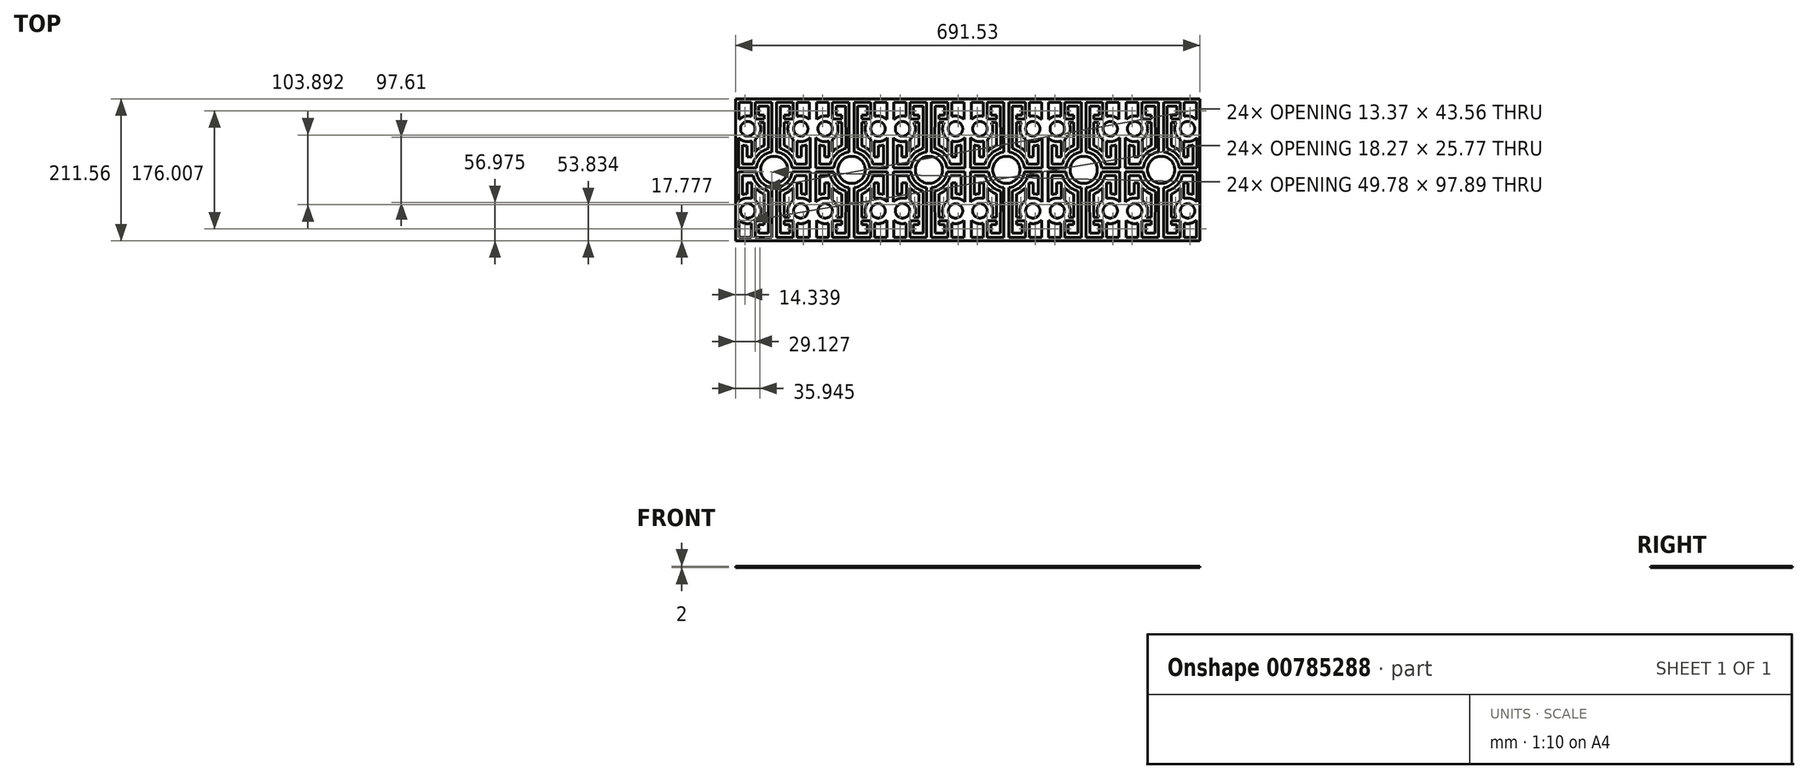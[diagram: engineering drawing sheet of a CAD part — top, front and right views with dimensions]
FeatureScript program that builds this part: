
annotation { "Feature Type Name" : "Feature", "Feature Type Description" : "" }
export const myFeature = defineFeature(function(context is Context, id is Id, definition is map)
    precondition{}
    {
        {
            var Q0;
            Q0=qCreatedBy(makeId("Top.planeOp"),FACE);
            var sketch = newSketch(context, id + "F0", { "sketchPlane" : qUnion([Q0])});
            skLineSegment(sketch, "E0.MirrorCS", {"start": v(61.19, -105.78) * mm, "end": v(-54.07, -105.78) * mm});
            skLineSegment(sketch, "E1.MirrorCS", {"start": v(-54.07, -105.78) * mm, "end": v(-54.07, 105.78) * mm});
            skLineSegment(sketch, "E2.MirrorCS", {"start": v(-54.07, 105.78) * mm, "end": v(-54.07, -105.78) * mm});
            skLineSegment(sketch, "E3.MirrorCS", {"start": v(61.19, 105.78) * mm, "end": v(-54.07, 105.78) * mm});
            skLineSegment(sketch, "E4.MirrorCS", {"start": v(-11.44, 75.88) * mm, "end": v(-11.44, 81.85) * mm});
            skLineSegment(sketch, "E5.MirrorCS", {"start": v(18.56, -75.88) * mm, "end": v(31.94, -75.88) * mm});
            skLineSegment(sketch, "E6.MirrorCS", {"start": v(-36.6, -19.6) * mm, "end": v(-30.12, -19.6) * mm});
            skArc(sketch, "E7.MirrorCS", {"start": v(43.73, 35.72) * mm, "mid": v(47.48, 36.1) * mm, "end": v(51.14, 37.04) * mm});
            skLineSegment(sketch, "E8.MirrorCS", {"start": v(43.73, 19.6) * mm, "end": v(37.24, 19.6) * mm});
            skLineSegment(sketch, "E9.MirrorCS", {"start": v(-19.53, 70.59) * mm, "end": v(-11.44, 70.59) * mm});
            skLineSegment(sketch, "E10.MirrorCS", {"start": v(-36.6, 19.6) * mm, "end": v(-30.12, 19.6) * mm});
            skArc(sketch, "E11.MirrorCS", {"start": v(43.73, -35.72) * mm, "mid": v(47.48, -36.1) * mm, "end": v(51.14, -37.04) * mm});
            skLineSegment(sketch, "E12.MirrorCS", {"start": v(-11.44, 75.88) * mm, "end": v(-24.82, 75.88) * mm});
            skArc(sketch, "E13.MirrorCS", {"start": v(-36.6, 35.72) * mm, "mid": v(-40.36, 36.1) * mm, "end": v(-44.02, 37.04) * mm});
            skLineSegment(sketch, "E14.MirrorCS", {"start": v(18.56, 75.88) * mm, "end": v(31.94, 75.88) * mm});
            skLineSegment(sketch, "E15.MirrorCS", {"start": v(31.94, -100.89) * mm, "end": v(31.94, -75.88) * mm});
            skLineSegment(sketch, "E16.MirrorCS", {"start": v(18.56, 75.88) * mm, "end": v(18.56, 81.85) * mm});
            skLineSegment(sketch, "E17.MirrorCS", {"start": v(-11.44, -75.88) * mm, "end": v(-11.44, -81.85) * mm});
            skLineSegment(sketch, "E18.MirrorCS", {"start": v(26.65, 70.59) * mm, "end": v(18.56, 70.59) * mm});
            skLineSegment(sketch, "E19.MirrorCS", {"start": v(26.67, 81.85) * mm, "end": v(18.56, 81.85) * mm});
            skLineSegment(sketch, "E20.MirrorCS", {"start": v(-19.55, -81.85) * mm, "end": v(-11.44, -81.85) * mm});
            skLineSegment(sketch, "E21.MirrorCS", {"start": v(18.56, -75.88) * mm, "end": v(18.56, -81.85) * mm});
            skLineSegment(sketch, "E22.MirrorCS", {"start": v(-19.53, -70.59) * mm, "end": v(-11.44, -70.59) * mm});
            skArc(sketch, "E23.MirrorCS", {"start": v(-36.6, -35.72) * mm, "mid": v(-40.36, -36.1) * mm, "end": v(-44.02, -37.04) * mm});
            skLineSegment(sketch, "E24.MirrorCS", {"start": v(-11.44, -75.88) * mm, "end": v(-24.82, -75.88) * mm});
            skLineSegment(sketch, "E25.MirrorCS", {"start": v(-19.55, -81.85) * mm, "end": v(-19.55, -94.64) * mm});
            skLineSegment(sketch, "E26.MirrorCS", {"start": v(-19.55, 94.64) * mm, "end": v(-5.34, 94.64) * mm});
            skLineSegment(sketch, "E27.MirrorCS", {"start": v(26.67, -81.85) * mm, "end": v(26.67, -94.64) * mm});
            skLineSegment(sketch, "E28.MirrorCS", {"start": v(-19.55, -94.64) * mm, "end": v(-5.34, -94.64) * mm});
            skLineSegment(sketch, "E29.MirrorCS", {"start": v(-19.55, 81.85) * mm, "end": v(-11.44, 81.85) * mm});
            skLineSegment(sketch, "E30.MirrorCS", {"start": v(26.67, 81.85) * mm, "end": v(26.67, 94.64) * mm});
            skLineSegment(sketch, "E31.MirrorCS", {"start": v(-19.55, 81.85) * mm, "end": v(-19.55, 94.64) * mm});
            skLineSegment(sketch, "E32.MirrorCS", {"start": v(43.73, -19.6) * mm, "end": v(37.24, -19.6) * mm});
            skLineSegment(sketch, "E33.MirrorCS", {"start": v(31.94, 100.89) * mm, "end": v(31.94, 75.88) * mm});
            skLineSegment(sketch, "E34.MirrorCS", {"start": v(26.65, -70.59) * mm, "end": v(18.56, -70.59) * mm});
            skLineSegment(sketch, "E35.MirrorCS", {"start": v(26.67, -81.85) * mm, "end": v(18.56, -81.85) * mm});
            skLineSegment(sketch, "E36.MirrorCS", {"start": v(-48.87, 100.89) * mm, "end": v(-30.6, 100.89) * mm});
            skArc(sketch, "E37.MirrorCS", {"start": v(-30.6, 79.48) * mm, "mid": v(-40.3, 79.71) * mm, "end": v(-48.87, 75.12) * mm});
            skLineSegment(sketch, "E38.MirrorCS", {"start": v(-30.6, 79.48) * mm, "end": v(-30.6, 100.89) * mm});
            skLineSegment(sketch, "E39.MirrorCS", {"start": v(-24.82, 100.89) * mm, "end": v(-24.82, 75.88) * mm});
            skLineSegment(sketch, "E40.MirrorCS", {"start": v(31.94, 100.89) * mm, "end": v(7.17, 100.89) * mm});
            skLineSegment(sketch, "E41.MirrorCS", {"start": v(-24.82, -100.89) * mm, "end": v(-24.82, -75.88) * mm});
            skLineSegment(sketch, "E42.MirrorCS", {"start": v(37.24, 42.87) * mm, "end": v(37.24, 19.6) * mm});
            skArc(sketch, "E43.MirrorCS", {"start": v(18.56, -36.2) * mm, "mid": v(25.73, -32.32) * mm, "end": v(31.93, -27.02) * mm});
            skLineSegment(sketch, "E44.MirrorCS", {"start": v(56.95, -47.98) * mm, "end": v(56.95, -3) * mm});
            skCircle(sketch, "E45.MirrorC", {"center": v(-35.89, 61.2) * mm, "radius": 10.77 * mm});
            skLineSegment(sketch, "E46.MirrorCS", {"start": v(-30.6, -79.48) * mm, "end": v(-30.6, -100.89) * mm});
            skLineSegment(sketch, "E47.MirrorCS", {"start": v(-30.12, 42.87) * mm, "end": v(-30.12, 19.6) * mm});
            skArc(sketch, "E48.MirrorCS", {"start": v(35.31, 8.78) * mm, "mid": v(26.82, 23.35) * mm, "end": v(12.23, 31.82) * mm});
            skLineSegment(sketch, "E49.MirrorCS", {"start": v(-0.05, -26.62) * mm, "end": v(-0.05, -100.89) * mm});
            skArc(sketch, "E50.MirrorCS", {"start": v(7.17, -26.62) * mm, "mid": v(22.75, -18.77) * mm, "end": v(30.21, -3) * mm});
            skLineSegment(sketch, "E51.MirrorCS", {"start": v(26.67, 94.64) * mm, "end": v(12.46, 94.64) * mm});
            skLineSegment(sketch, "E52.MirrorCS", {"start": v(-28.2, 8.78) * mm, "end": v(-44.02, 8.78) * mm});
            skLineSegment(sketch, "E53.MirrorCS", {"start": v(55.99, 100.89) * mm, "end": v(37.72, 100.89) * mm});
            skLineSegment(sketch, "E54.MirrorCS", {"start": v(43.73, 19.6) * mm, "end": v(43.73, 35.72) * mm});
            skLineSegment(sketch, "E55.MirrorCS", {"start": v(30.21, -3) * mm, "end": v(56.95, -3) * mm});
            skArc(sketch, "E56.MirrorCS", {"start": v(37.72, 79.48) * mm, "mid": v(47.43, 79.71) * mm, "end": v(55.99, 75.12) * mm});
            skLineSegment(sketch, "E57.MirrorCS", {"start": v(-24.82, -100.89) * mm, "end": v(-0.05, -100.89) * mm});
            skLineSegment(sketch, "E58.MirrorCS", {"start": v(-11.44, 70.59) * mm, "end": v(-11.44, 36.2) * mm});
            skLineSegment(sketch, "E59.MirrorCS", {"start": v(12.46, 94.64) * mm, "end": v(12.23, 31.81) * mm});
            skArc(sketch, "E60.MirrorCS", {"start": v(-24.81, 45.33) * mm, "mid": v(-17.03, 56.84) * mm, "end": v(-18.96, 70.59) * mm});
            skLineSegment(sketch, "E61.MirrorCS", {"start": v(-5.34, 94.64) * mm, "end": v(-5.1, 31.81) * mm});
            skLineSegment(sketch, "E62.MirrorCS", {"start": v(35.31, -8.78) * mm, "end": v(51.14, -8.78) * mm});
            skArc(sketch, "E63.MirrorCS", {"start": v(-28.2, 8.78) * mm, "mid": v(-19.7, 23.35) * mm, "end": v(-5.1, 31.82) * mm});
            skLineSegment(sketch, "E64.MirrorCS", {"start": v(37.72, -79.48) * mm, "end": v(37.72, -100.89) * mm});
            skLineSegment(sketch, "E65.MirrorCS", {"start": v(-24.81, -27.02) * mm, "end": v(-24.81, -45.33) * mm});
            skCircle(sketch, "E66.MirrorC", {"center": v(43, -61.2) * mm, "radius": 10.77 * mm});
            skLineSegment(sketch, "E67.MirrorCS", {"start": v(31.94, -100.89) * mm, "end": v(7.17, -100.89) * mm});
            skLineSegment(sketch, "E68.MirrorCS", {"start": v(-48.87, -100.89) * mm, "end": v(-30.6, -100.89) * mm});
            skLineSegment(sketch, "E69.MirrorCS", {"start": v(-30.12, -42.87) * mm, "end": v(-30.12, -19.6) * mm});
            skLineSegment(sketch, "E70.MirrorCS", {"start": v(51.14, -37.04) * mm, "end": v(51.14, -8.78) * mm});
            skLineSegment(sketch, "E71.MirrorCS", {"start": v(51.14, 37.04) * mm, "end": v(51.14, 8.78) * mm});
            skLineSegment(sketch, "E72.MirrorCS", {"start": v(7.17, 26.62) * mm, "end": v(7.17, 100.89) * mm});
            skLineSegment(sketch, "E73.MirrorCS", {"start": v(-24.81, 27.02) * mm, "end": v(-24.81, 45.33) * mm});
            skLineSegment(sketch, "E74.MirrorCS", {"start": v(-36.6, 19.6) * mm, "end": v(-36.6, 35.72) * mm});
            skLineSegment(sketch, "E75.MirrorCS", {"start": v(56.95, 47.98) * mm, "end": v(56.95, 3) * mm});
            skLineSegment(sketch, "E76.MirrorCS", {"start": v(55.99, -75.12) * mm, "end": v(55.99, -100.89) * mm});
            skArc(sketch, "E77.MirrorCS", {"start": v(-11.44, 36.2) * mm, "mid": v(-18.6, 32.32) * mm, "end": v(-24.81, 27.02) * mm});
            skArc(sketch, "E78.MirrorCS", {"start": v(-0.05, 26.62) * mm, "mid": v(-15.63, 18.77) * mm, "end": v(-23.1, 3) * mm});
            skLineSegment(sketch, "E79.MirrorCS", {"start": v(55.99, 75.12) * mm, "end": v(55.99, 100.89) * mm});
            skArc(sketch, "E80.MirrorCS", {"start": v(31.93, 45.33) * mm, "mid": v(24.15, 56.84) * mm, "end": v(26.08, 70.59) * mm});
            skLineSegment(sketch, "E81.MirrorCS", {"start": v(-24.82, 100.89) * mm, "end": v(-0.05, 100.89) * mm});
            skLineSegment(sketch, "E82.MirrorCS", {"start": v(-5.34, -94.64) * mm, "end": v(-5.1, -31.81) * mm});
            skLineSegment(sketch, "E83.MirrorCS", {"start": v(31.93, 27.02) * mm, "end": v(31.93, 45.33) * mm});
            skArc(sketch, "E84.MirrorCS", {"start": v(35.31, -8.78) * mm, "mid": v(26.82, -23.35) * mm, "end": v(12.23, -31.82) * mm});
            skArc(sketch, "E85.MirrorCS", {"start": v(7.17, 26.62) * mm, "mid": v(22.75, 18.77) * mm, "end": v(30.21, 3) * mm});
            skArc(sketch, "E86.MirrorCS", {"start": v(-24.81, -45.33) * mm, "mid": v(-17.03, -56.84) * mm, "end": v(-18.96, -70.59) * mm});
            skCircle(sketch, "E87.MirrorC", {"center": v(-35.89, -61.2) * mm, "radius": 10.77 * mm});
            skArc(sketch, "E88.MirrorCS", {"start": v(56.95, 47.98) * mm, "mid": v(47.83, 42.6) * mm, "end": v(37.24, 42.87) * mm});
            skLineSegment(sketch, "E89.MirrorCS", {"start": v(37.24, -42.87) * mm, "end": v(37.24, -19.6) * mm});
            skLineSegment(sketch, "E90.MirrorCS", {"start": v(-23.1, 3) * mm, "end": v(-49.83, 3) * mm});
            skLineSegment(sketch, "E91.MirrorCS", {"start": v(55.99, -100.89) * mm, "end": v(37.72, -100.89) * mm});
            skLineSegment(sketch, "E92.MirrorCS", {"start": v(-48.87, 75.12) * mm, "end": v(-48.87, 100.89) * mm});
            skLineSegment(sketch, "E93.MirrorCS", {"start": v(37.72, 79.48) * mm, "end": v(37.72, 100.89) * mm});
            skLineSegment(sketch, "E94.MirrorCS", {"start": v(-23.1, -3) * mm, "end": v(-49.83, -3) * mm});
            skArc(sketch, "E95.MirrorCS", {"start": v(37.72, -79.48) * mm, "mid": v(47.43, -79.71) * mm, "end": v(55.99, -75.12) * mm});
            skLineSegment(sketch, "E96.MirrorCS", {"start": v(43.73, -19.6) * mm, "end": v(43.73, -35.72) * mm});
            skLineSegment(sketch, "E97.MirrorCS", {"start": v(-49.83, 47.98) * mm, "end": v(-49.83, 3) * mm});
            skArc(sketch, "E98.MirrorCS", {"start": v(56.95, -47.98) * mm, "mid": v(47.83, -42.6) * mm, "end": v(37.24, -42.87) * mm});
            skLineSegment(sketch, "E99.MirrorCS", {"start": v(7.17, -26.62) * mm, "end": v(7.17, -100.89) * mm});
            skLineSegment(sketch, "E100.MirrorCS", {"start": v(12.46, -94.64) * mm, "end": v(12.23, -31.81) * mm});
            skLineSegment(sketch, "E101.MirrorCS", {"start": v(-44.02, -37.04) * mm, "end": v(-44.02, -8.78) * mm});
            skArc(sketch, "E102.MirrorCS", {"start": v(18.56, 36.2) * mm, "mid": v(25.73, 32.32) * mm, "end": v(31.93, 27.02) * mm});
            skLineSegment(sketch, "E103.MirrorCS", {"start": v(35.31, 8.78) * mm, "end": v(51.14, 8.78) * mm});
            skLineSegment(sketch, "E104.MirrorCS", {"start": v(-36.6, -19.6) * mm, "end": v(-36.6, -35.72) * mm});
            skArc(sketch, "E105.MirrorCS", {"start": v(-11.44, -36.2) * mm, "mid": v(-18.6, -32.32) * mm, "end": v(-24.81, -27.02) * mm});
            skLineSegment(sketch, "E106.MirrorCS", {"start": v(-28.2, -8.78) * mm, "end": v(-44.02, -8.78) * mm});
            skLineSegment(sketch, "E107.MirrorCS", {"start": v(-11.44, -70.59) * mm, "end": v(-11.44, -36.2) * mm});
            skLineSegment(sketch, "E108.MirrorCS", {"start": v(-49.83, -47.98) * mm, "end": v(-49.83, -3) * mm});
            skCircle(sketch, "E109.MirrorC", {"center": v(43, 61.2) * mm, "radius": 10.77 * mm});
            skLineSegment(sketch, "E110.MirrorCS", {"start": v(26.67, -94.64) * mm, "end": v(12.46, -94.64) * mm});
            skLineSegment(sketch, "E111.MirrorCS", {"start": v(-44.02, 37.04) * mm, "end": v(-44.02, 8.78) * mm});
            skArc(sketch, "E112.MirrorCS", {"start": v(31.93, -45.33) * mm, "mid": v(24.15, -56.84) * mm, "end": v(26.08, -70.59) * mm});
            skArc(sketch, "E113.MirrorCS", {"start": v(-49.83, -47.98) * mm, "mid": v(-40.7, -42.6) * mm, "end": v(-30.12, -42.87) * mm});
            skLineSegment(sketch, "E114.MirrorCS", {"start": v(-48.87, -75.12) * mm, "end": v(-48.87, -100.89) * mm});
            skArc(sketch, "E115.MirrorCS", {"start": v(-0.05, -26.62) * mm, "mid": v(-15.63, -18.77) * mm, "end": v(-23.1, -3) * mm});
            skLineSegment(sketch, "E116.MirrorCS", {"start": v(18.56, 70.59) * mm, "end": v(18.56, 36.2) * mm});
            skArc(sketch, "E117.MirrorCS", {"start": v(-30.6, -79.48) * mm, "mid": v(-40.3, -79.71) * mm, "end": v(-48.87, -75.12) * mm});
            skLineSegment(sketch, "E118.MirrorCS", {"start": v(30.21, 3) * mm, "end": v(56.95, 3) * mm});
            skLineSegment(sketch, "E119.MirrorCS", {"start": v(18.56, -70.59) * mm, "end": v(18.56, -36.2) * mm});
            skLineSegment(sketch, "E120.MirrorCS", {"start": v(31.93, -27.02) * mm, "end": v(31.93, -45.33) * mm});
            skArc(sketch, "E121.MirrorCS", {"start": v(-49.83, 47.98) * mm, "mid": v(-40.7, 42.6) * mm, "end": v(-30.12, 42.87) * mm});
            skArc(sketch, "E122.MirrorCS", {"start": v(-28.2, -8.78) * mm, "mid": v(-19.7, -23.35) * mm, "end": v(-5.1, -31.82) * mm});
            skLineSegment(sketch, "E123.MirrorCS", {"start": v(-0.05, 26.62) * mm, "end": v(-0.05, 100.89) * mm});
            skCircle(sketch, "E124.MirrorC", {"center": v(3.56, 0) * mm, "radius": 20.2 * mm});
            skLineSegment(sketch, "E125.MirrorCS", {"start": v(-284.58, 105.78) * mm, "end": v(-284.58, -105.78) * mm});
            skLineSegment(sketch, "E126.MirrorCS", {"start": v(-284.58, -105.78) * mm, "end": v(-284.58, 105.78) * mm});
            skLineSegment(sketch, "E127.MirrorCS", {"start": v(-241.95, 75.88) * mm, "end": v(-241.95, 81.85) * mm});
            skLineSegment(sketch, "E128.MirrorCS", {"start": v(-211.95, 75.88) * mm, "end": v(-211.95, 81.85) * mm});
            skLineSegment(sketch, "E129.MirrorCS", {"start": v(-126.7, 75.88) * mm, "end": v(-126.7, 81.85) * mm});
            skLineSegment(sketch, "E130.MirrorCS", {"start": v(-241.95, -75.88) * mm, "end": v(-241.95, -81.85) * mm});
            skLineSegment(sketch, "E131.MirrorCS", {"start": v(-71.53, -19.6) * mm, "end": v(-78.02, -19.6) * mm});
            skLineSegment(sketch, "E132.MirrorCS", {"start": v(-255.33, -100.89) * mm, "end": v(-255.33, -75.88) * mm});
            skArc(sketch, "E133.MirrorCS", {"start": v(-71.53, 35.72) * mm, "mid": v(-67.77, 36.1) * mm, "end": v(-64.11, 37.04) * mm});
            skLineSegment(sketch, "E134.MirrorCS", {"start": v(-134.8, 81.85) * mm, "end": v(-126.7, 81.85) * mm});
            skArc(sketch, "E135.MirrorCS", {"start": v(-151.86, 35.72) * mm, "mid": v(-155.62, 36.1) * mm, "end": v(-159.28, 37.04) * mm});
            skLineSegment(sketch, "E136.MirrorCS", {"start": v(-250.06, -81.85) * mm, "end": v(-250.06, -94.64) * mm});
            skLineSegment(sketch, "E137.MirrorCS", {"start": v(-71.53, 19.6) * mm, "end": v(-78.02, 19.6) * mm});
            skLineSegment(sketch, "E138.MirrorCS", {"start": v(-88.6, 70.59) * mm, "end": v(-96.7, 70.59) * mm});
            skArc(sketch, "E139.MirrorCS", {"start": v(-71.53, -35.72) * mm, "mid": v(-67.77, -36.1) * mm, "end": v(-64.11, -37.04) * mm});
            skArc(sketch, "E140.MirrorCS", {"start": v(-151.86, -35.72) * mm, "mid": v(-155.62, -36.1) * mm, "end": v(-159.28, -37.04) * mm});
            skLineSegment(sketch, "E141.MirrorCS", {"start": v(-134.8, -81.85) * mm, "end": v(-126.7, -81.85) * mm});
            skLineSegment(sketch, "E142.MirrorCS", {"start": v(-126.7, -75.88) * mm, "end": v(-126.7, -81.85) * mm});
            skLineSegment(sketch, "E143.MirrorCS", {"start": v(-186.78, 19.6) * mm, "end": v(-193.27, 19.6) * mm});
            skLineSegment(sketch, "E144.MirrorCS", {"start": v(-203.84, -81.85) * mm, "end": v(-203.84, -94.64) * mm});
            skArc(sketch, "E145.MirrorCS", {"start": v(-267.12, 35.72) * mm, "mid": v(-270.87, 36.1) * mm, "end": v(-274.53, 37.04) * mm});
            skLineSegment(sketch, "E146.MirrorCS", {"start": v(-211.95, -75.88) * mm, "end": v(-211.95, -81.85) * mm});
            skArc(sketch, "E147.MirrorCS", {"start": v(-267.12, -35.72) * mm, "mid": v(-270.87, -36.1) * mm, "end": v(-274.53, -37.04) * mm});
            skLineSegment(sketch, "E148.MirrorCS", {"start": v(-134.79, 70.59) * mm, "end": v(-126.7, 70.59) * mm});
            skLineSegment(sketch, "E149.MirrorCS", {"start": v(-96.7, -75.88) * mm, "end": v(-83.31, -75.88) * mm});
            skLineSegment(sketch, "E150.MirrorCS", {"start": v(-88.6, -70.59) * mm, "end": v(-96.7, -70.59) * mm});
            skLineSegment(sketch, "E151.MirrorCS", {"start": v(-96.7, -75.88) * mm, "end": v(-96.7, -81.85) * mm});
            skLineSegment(sketch, "E152.MirrorCS", {"start": v(-134.8, -81.85) * mm, "end": v(-134.8, -94.64) * mm});
            skLineSegment(sketch, "E153.MirrorCS", {"start": v(-88.58, -81.85) * mm, "end": v(-88.58, -94.64) * mm});
            skLineSegment(sketch, "E154.MirrorCS", {"start": v(-151.86, -19.6) * mm, "end": v(-145.37, -19.6) * mm});
            skLineSegment(sketch, "E155.MirrorCS", {"start": v(-126.7, -75.88) * mm, "end": v(-140.08, -75.88) * mm});
            skLineSegment(sketch, "E156.MirrorCS", {"start": v(-96.7, 75.88) * mm, "end": v(-96.7, 81.85) * mm});
            skArc(sketch, "E157.MirrorCS", {"start": v(-186.78, -35.72) * mm, "mid": v(-183.03, -36.1) * mm, "end": v(-179.37, -37.04) * mm});
            skLineSegment(sketch, "E158.MirrorCS", {"start": v(-88.58, -81.85) * mm, "end": v(-96.7, -81.85) * mm});
            skLineSegment(sketch, "E159.MirrorCS", {"start": v(-134.79, -70.59) * mm, "end": v(-126.7, -70.59) * mm});
            skLineSegment(sketch, "E160.MirrorCS", {"start": v(-250.06, -81.85) * mm, "end": v(-241.95, -81.85) * mm});
            skArc(sketch, "E161.MirrorCS", {"start": v(-186.78, 35.72) * mm, "mid": v(-183.03, 36.1) * mm, "end": v(-179.37, 37.04) * mm});
            skLineSegment(sketch, "E162.MirrorCS", {"start": v(-186.78, -19.6) * mm, "end": v(-193.27, -19.6) * mm});
            skLineSegment(sketch, "E163.MirrorCS", {"start": v(-96.7, 75.88) * mm, "end": v(-83.31, 75.88) * mm});
            skLineSegment(sketch, "E164.MirrorCS", {"start": v(-198.57, -100.89) * mm, "end": v(-198.57, -75.88) * mm});
            skLineSegment(sketch, "E165.MirrorCS", {"start": v(-126.7, 75.88) * mm, "end": v(-140.08, 75.88) * mm});
            skLineSegment(sketch, "E166.MirrorCS", {"start": v(-88.58, 81.85) * mm, "end": v(-96.7, 81.85) * mm});
            skLineSegment(sketch, "E167.MirrorCS", {"start": v(-151.86, 19.6) * mm, "end": v(-145.37, 19.6) * mm});
            skLineSegment(sketch, "E168.MirrorCS", {"start": v(-203.84, -81.85) * mm, "end": v(-211.95, -81.85) * mm});
            skLineSegment(sketch, "E169.MirrorCS", {"start": v(-267.12, 19.6) * mm, "end": v(-260.63, 19.6) * mm});
            skLineSegment(sketch, "E170.MirrorCS", {"start": v(-267.12, -19.6) * mm, "end": v(-260.63, -19.6) * mm});
            skLineSegment(sketch, "E171.MirrorCS", {"start": v(-250.06, 81.85) * mm, "end": v(-241.95, 81.85) * mm});
            skLineSegment(sketch, "E172.MirrorCS", {"start": v(-203.84, 81.85) * mm, "end": v(-211.95, 81.85) * mm});
            skLineSegment(sketch, "E173.MirrorCS", {"start": v(-211.95, 75.88) * mm, "end": v(-198.57, 75.88) * mm});
            skLineSegment(sketch, "E174.MirrorCS", {"start": v(-211.95, -75.88) * mm, "end": v(-198.57, -75.88) * mm});
            skLineSegment(sketch, "E175.MirrorCS", {"start": v(-203.86, 70.59) * mm, "end": v(-211.95, 70.59) * mm});
            skLineSegment(sketch, "E176.MirrorCS", {"start": v(-203.86, -70.59) * mm, "end": v(-211.95, -70.59) * mm});
            skLineSegment(sketch, "E177.MirrorCS", {"start": v(-250.04, -70.59) * mm, "end": v(-241.95, -70.59) * mm});
            skLineSegment(sketch, "E178.MirrorCS", {"start": v(-241.95, -75.88) * mm, "end": v(-255.33, -75.88) * mm});
            skLineSegment(sketch, "E179.MirrorCS", {"start": v(-241.95, 75.88) * mm, "end": v(-255.33, 75.88) * mm});
            skLineSegment(sketch, "E180.MirrorCS", {"start": v(-250.04, 70.59) * mm, "end": v(-241.95, 70.59) * mm});
            skArc(sketch, "E181.MirrorCS", {"start": v(-108.08, -26.62) * mm, "mid": v(-92.5, -18.77) * mm, "end": v(-85.04, -3) * mm});
            skLineSegment(sketch, "E182.MirrorCS", {"start": v(-143.44, 8.78) * mm, "end": v(-159.28, 8.78) * mm});
            skLineSegment(sketch, "E183.MirrorCS", {"start": v(-102.8, -94.64) * mm, "end": v(-103.03, -31.81) * mm});
            skLineSegment(sketch, "E184.MirrorCS", {"start": v(-88.58, 94.64) * mm, "end": v(-102.8, 94.64) * mm});
            skLineSegment(sketch, "E185.MirrorCS", {"start": v(-159.28, 37.04) * mm, "end": v(-159.28, 8.78) * mm});
            skArc(sketch, "E186.MirrorCS", {"start": v(-192.8, 79.48) * mm, "mid": v(-183.08, 79.71) * mm, "end": v(-174.52, 75.12) * mm});
            skLineSegment(sketch, "E187.MirrorCS", {"start": v(-174.52, 100.89) * mm, "end": v(-192.8, 100.89) * mm});
            skLineSegment(sketch, "E188.MirrorCS", {"start": v(-85.04, 3) * mm, "end": v(-58.3, 3) * mm});
            skLineSegment(sketch, "E189.MirrorCS", {"start": v(-218.05, 94.64) * mm, "end": v(-218.28, 31.81) * mm});
            skLineSegment(sketch, "E190.MirrorCS", {"start": v(-241.95, -70.59) * mm, "end": v(-241.95, -36.2) * mm});
            skLineSegment(sketch, "E191.MirrorCS", {"start": v(-134.8, 81.85) * mm, "end": v(-134.8, 94.64) * mm});
            skLineSegment(sketch, "E192.MirrorCS", {"start": v(-140.08, 100.89) * mm, "end": v(-115.3, 100.89) * mm});
            skArc(sketch, "E193.MirrorCS", {"start": v(-241.95, -36.2) * mm, "mid": v(-249.12, -32.32) * mm, "end": v(-255.32, -27.02) * mm});
            skLineSegment(sketch, "E194.MirrorCS", {"start": v(-260.63, -42.87) * mm, "end": v(-260.63, -19.6) * mm});
            skLineSegment(sketch, "E195.MirrorCS", {"start": v(-211.95, 70.59) * mm, "end": v(-211.95, 36.2) * mm});
            skLineSegment(sketch, "E196.MirrorCS", {"start": v(-235.85, -94.64) * mm, "end": v(-235.62, -31.81) * mm});
            skLineSegment(sketch, "E197.MirrorCS", {"start": v(-230.56, -26.62) * mm, "end": v(-230.56, -100.89) * mm});
            skCircle(sketch, "E198.MirrorC", {"center": v(-187.5, 61.2) * mm, "radius": 10.77 * mm});
            skArc(sketch, "E199.MirrorCS", {"start": v(-77.54, 79.48) * mm, "mid": v(-67.83, 79.71) * mm, "end": v(-59.27, 75.12) * mm});
            skLineSegment(sketch, "E200.MirrorCS", {"start": v(-88.58, 81.85) * mm, "end": v(-88.58, 94.64) * mm});
            skCircle(sketch, "E201.MirrorC", {"center": v(-266.4, -61.2) * mm, "radius": 10.77 * mm});
            skLineSegment(sketch, "E202.MirrorCS", {"start": v(-258.7, 8.78) * mm, "end": v(-274.53, 8.78) * mm});
            skLineSegment(sketch, "E203.MirrorCS", {"start": v(-140.08, -100.89) * mm, "end": v(-140.08, -75.88) * mm});
            skArc(sketch, "E204.MirrorCS", {"start": v(-255.32, 45.33) * mm, "mid": v(-247.54, 56.84) * mm, "end": v(-249.47, 70.59) * mm});
            skArc(sketch, "E205.MirrorCS", {"start": v(-173.55, 47.98) * mm, "mid": v(-182.68, 42.6) * mm, "end": v(-193.27, 42.87) * mm});
            skArc(sketch, "E206.MirrorCS", {"start": v(-258.7, -8.78) * mm, "mid": v(-250.2, -23.35) * mm, "end": v(-235.62, -31.82) * mm});
            skLineSegment(sketch, "E207.MirrorCS", {"start": v(-145.85, 79.48) * mm, "end": v(-145.85, 100.89) * mm});
            skArc(sketch, "E208.MirrorCS", {"start": v(-96.7, 36.2) * mm, "mid": v(-89.53, 32.32) * mm, "end": v(-83.32, 27.02) * mm});
            skLineSegment(sketch, "E209.MirrorCS", {"start": v(-102.8, 94.64) * mm, "end": v(-103.03, 31.81) * mm});
            skCircle(sketch, "E210.MirrorC", {"center": v(-72.25, 61.2) * mm, "radius": 10.77 * mm});
            skLineSegment(sketch, "E211.MirrorCS", {"start": v(-115.3, -26.62) * mm, "end": v(-115.3, -100.89) * mm});
            skLineSegment(sketch, "E212.MirrorCS", {"start": v(-186.78, -19.6) * mm, "end": v(-186.78, -35.72) * mm});
            skLineSegment(sketch, "E213.MirrorCS", {"start": v(-250.06, 94.64) * mm, "end": v(-235.85, 94.64) * mm});
            skArc(sketch, "E214.MirrorCS", {"start": v(-145.85, -79.48) * mm, "mid": v(-155.56, -79.71) * mm, "end": v(-164.12, -75.12) * mm});
            skLineSegment(sketch, "E215.MirrorCS", {"start": v(-164.12, -100.89) * mm, "end": v(-145.85, -100.89) * mm});
            skLineSegment(sketch, "E216.MirrorCS", {"start": v(-140.08, -100.89) * mm, "end": v(-115.3, -100.89) * mm});
            skLineSegment(sketch, "E217.MirrorCS", {"start": v(-59.27, -100.89) * mm, "end": v(-77.54, -100.89) * mm});
            skLineSegment(sketch, "E218.MirrorCS", {"start": v(-267.12, -19.6) * mm, "end": v(-267.12, -35.72) * mm});
            skLineSegment(sketch, "E219.MirrorCS", {"start": v(-198.57, 100.89) * mm, "end": v(-223.34, 100.89) * mm});
            skLineSegment(sketch, "E220.MirrorCS", {"start": v(-174.52, 75.12) * mm, "end": v(-174.52, 100.89) * mm});
            skLineSegment(sketch, "E221.MirrorCS", {"start": v(-138.35, 3) * mm, "end": v(-165.09, 3) * mm});
            skCircle(sketch, "E222.MirrorC", {"center": v(-72.25, -61.2) * mm, "radius": 10.77 * mm});
            skLineSegment(sketch, "E223.MirrorCS", {"start": v(-164.12, -75.12) * mm, "end": v(-164.12, -100.89) * mm});
            skLineSegment(sketch, "E224.MirrorCS", {"start": v(-140.07, -27.02) * mm, "end": v(-140.07, -45.33) * mm});
            skLineSegment(sketch, "E225.MirrorCS", {"start": v(-145.37, -42.87) * mm, "end": v(-145.37, -19.6) * mm});
            skLineSegment(sketch, "E226.MirrorCS", {"start": v(-280.34, -47.98) * mm, "end": v(-280.34, -3) * mm});
            skLineSegment(sketch, "E227.MirrorCS", {"start": v(-164.12, 75.12) * mm, "end": v(-164.12, 100.89) * mm});
            skArc(sketch, "E228.MirrorCS", {"start": v(-211.95, 36.2) * mm, "mid": v(-204.78, 32.32) * mm, "end": v(-198.58, 27.02) * mm});
            skArc(sketch, "E229.MirrorCS", {"start": v(-79.94, 8.78) * mm, "mid": v(-88.44, 23.35) * mm, "end": v(-103.03, 31.82) * mm});
            skLineSegment(sketch, "E230.MirrorCS", {"start": v(-78.02, 42.87) * mm, "end": v(-78.02, 19.6) * mm});
            skLineSegment(sketch, "E231.MirrorCS", {"start": v(-218.05, -94.64) * mm, "end": v(-218.28, -31.81) * mm});
            skLineSegment(sketch, "E232.MirrorCS", {"start": v(-151.86, 19.6) * mm, "end": v(-151.86, 35.72) * mm});
            skArc(sketch, "E233.MirrorCS", {"start": v(-145.85, 79.48) * mm, "mid": v(-155.56, 79.71) * mm, "end": v(-164.12, 75.12) * mm});
            skLineSegment(sketch, "E234.MirrorCS", {"start": v(-96.7, -70.59) * mm, "end": v(-96.7, -36.2) * mm});
            skLineSegment(sketch, "E235.MirrorCS", {"start": v(-64.11, 37.04) * mm, "end": v(-64.11, 8.78) * mm});
            skLineSegment(sketch, "E236.MirrorCS", {"start": v(-138.35, -3) * mm, "end": v(-165.09, -3) * mm});
            skLineSegment(sketch, "E237.MirrorCS", {"start": v(-165.09, 47.98) * mm, "end": v(-165.09, 3) * mm});
            skLineSegment(sketch, "E238.MirrorCS", {"start": v(-200.3, -3) * mm, "end": v(-173.55, -3) * mm});
            skArc(sketch, "E239.MirrorCS", {"start": v(-241.95, 36.2) * mm, "mid": v(-249.12, 32.32) * mm, "end": v(-255.32, 27.02) * mm});
            skLineSegment(sketch, "E240.MirrorCS", {"start": v(-83.32, 27.02) * mm, "end": v(-83.32, 45.33) * mm});
            skLineSegment(sketch, "E241.MirrorCS", {"start": v(-261.1, 79.48) * mm, "end": v(-261.1, 100.89) * mm});
            skArc(sketch, "E242.MirrorCS", {"start": v(-173.55, -47.98) * mm, "mid": v(-182.68, -42.6) * mm, "end": v(-193.27, -42.87) * mm});
            skLineSegment(sketch, "E243.MirrorCS", {"start": v(-255.33, 100.89) * mm, "end": v(-230.56, 100.89) * mm});
            skLineSegment(sketch, "E244.MirrorCS", {"start": v(-250.06, -94.64) * mm, "end": v(-235.85, -94.64) * mm});
            skArc(sketch, "E245.MirrorCS", {"start": v(-192.8, -79.48) * mm, "mid": v(-183.08, -79.71) * mm, "end": v(-174.52, -75.12) * mm});
            skLineSegment(sketch, "E246.MirrorCS", {"start": v(-203.84, -94.64) * mm, "end": v(-218.05, -94.64) * mm});
            skLineSegment(sketch, "E247.MirrorCS", {"start": v(-230.56, 26.62) * mm, "end": v(-230.56, 100.89) * mm});
            skArc(sketch, "E248.MirrorCS", {"start": v(-115.3, 26.62) * mm, "mid": v(-130.89, 18.77) * mm, "end": v(-138.35, 3) * mm});
            skLineSegment(sketch, "E249.MirrorCS", {"start": v(-59.27, 75.12) * mm, "end": v(-59.27, 100.89) * mm});
            skLineSegment(sketch, "E250.MirrorCS", {"start": v(-134.8, 94.64) * mm, "end": v(-120.6, 94.64) * mm});
            skLineSegment(sketch, "E251.MirrorCS", {"start": v(-140.07, 27.02) * mm, "end": v(-140.07, 45.33) * mm});
            skArc(sketch, "E252.MirrorCS", {"start": v(-195.2, 8.78) * mm, "mid": v(-203.69, 23.35) * mm, "end": v(-218.28, 31.82) * mm});
            skCircle(sketch, "E253.MirrorC", {"center": v(-187.5, -61.2) * mm, "radius": 10.77 * mm});
            skArc(sketch, "E254.MirrorCS", {"start": v(-230.56, -26.62) * mm, "mid": v(-246.14, -18.77) * mm, "end": v(-253.6, -3) * mm});
            skArc(sketch, "E255.MirrorCS", {"start": v(-280.34, -47.98) * mm, "mid": v(-271.22, -42.6) * mm, "end": v(-260.63, -42.87) * mm});
            skLineSegment(sketch, "E256.MirrorCS", {"start": v(-280.34, 47.98) * mm, "end": v(-280.34, 3) * mm});
            skLineSegment(sketch, "E257.MirrorCS", {"start": v(-179.37, -37.04) * mm, "end": v(-179.37, -8.78) * mm});
            skArc(sketch, "E258.MirrorCS", {"start": v(-280.34, 47.98) * mm, "mid": v(-271.22, 42.6) * mm, "end": v(-260.63, 42.87) * mm});
            skLineSegment(sketch, "E259.MirrorCS", {"start": v(-192.8, -79.48) * mm, "end": v(-192.8, -100.89) * mm});
            skLineSegment(sketch, "E260.MirrorCS", {"start": v(-108.08, -26.62) * mm, "end": v(-108.08, -100.89) * mm});
            skLineSegment(sketch, "E261.MirrorCS", {"start": v(-59.27, 100.89) * mm, "end": v(-77.54, 100.89) * mm});
            skLineSegment(sketch, "E262.MirrorCS", {"start": v(-85.04, -3) * mm, "end": v(-58.3, -3) * mm});
            skLineSegment(sketch, "E263.MirrorCS", {"start": v(-83.32, -27.02) * mm, "end": v(-83.32, -45.33) * mm});
            skLineSegment(sketch, "E264.MirrorCS", {"start": v(-173.55, 47.98) * mm, "end": v(-173.55, 3) * mm});
            skLineSegment(sketch, "E265.MirrorCS", {"start": v(-58.3, 47.98) * mm, "end": v(-58.3, 3) * mm});
            skLineSegment(sketch, "E266.MirrorCS", {"start": v(-200.3, 3) * mm, "end": v(-173.55, 3) * mm});
            skLineSegment(sketch, "E267.MirrorCS", {"start": v(-140.08, 100.89) * mm, "end": v(-140.08, 75.88) * mm});
            skLineSegment(sketch, "E268.MirrorCS", {"start": v(-255.33, -100.89) * mm, "end": v(-230.56, -100.89) * mm});
            skLineSegment(sketch, "E269.MirrorCS", {"start": v(-223.34, -26.62) * mm, "end": v(-223.34, -100.89) * mm});
            skArc(sketch, "E270.MirrorCS", {"start": v(-126.7, 36.2) * mm, "mid": v(-133.86, 32.32) * mm, "end": v(-140.07, 27.02) * mm});
            skArc(sketch, "E271.MirrorCS", {"start": v(-108.08, 26.62) * mm, "mid": v(-92.5, 18.77) * mm, "end": v(-85.04, 3) * mm});
            skLineSegment(sketch, "E272.MirrorCS", {"start": v(-115.3, 26.62) * mm, "end": v(-115.3, 100.89) * mm});
            skArc(sketch, "E273.MirrorCS", {"start": v(-58.3, 47.98) * mm, "mid": v(-67.43, 42.6) * mm, "end": v(-78.02, 42.87) * mm});
            skLineSegment(sketch, "E274.MirrorCS", {"start": v(-143.44, -8.78) * mm, "end": v(-159.28, -8.78) * mm});
            skLineSegment(sketch, "E275.MirrorCS", {"start": v(-274.53, 37.04) * mm, "end": v(-274.53, 8.78) * mm});
            skLineSegment(sketch, "E276.MirrorCS", {"start": v(-260.63, 42.87) * mm, "end": v(-260.63, 19.6) * mm});
            skLineSegment(sketch, "E277.MirrorCS", {"start": v(-258.7, -8.78) * mm, "end": v(-274.53, -8.78) * mm});
            skLineSegment(sketch, "E278.MirrorCS", {"start": v(-192.8, 79.48) * mm, "end": v(-192.8, 100.89) * mm});
            skLineSegment(sketch, "E279.MirrorCS", {"start": v(-267.12, 19.6) * mm, "end": v(-267.12, 35.72) * mm});
            skArc(sketch, "E280.MirrorCS", {"start": v(-77.54, -79.48) * mm, "mid": v(-67.83, -79.71) * mm, "end": v(-59.27, -75.12) * mm});
            skArc(sketch, "E281.MirrorCS", {"start": v(-126.7, -36.2) * mm, "mid": v(-133.86, -32.32) * mm, "end": v(-140.07, -27.02) * mm});
            skLineSegment(sketch, "E282.MirrorCS", {"start": v(-159.28, -37.04) * mm, "end": v(-159.28, -8.78) * mm});
            skLineSegment(sketch, "E283.MirrorCS", {"start": v(-173.55, -47.98) * mm, "end": v(-173.55, -3) * mm});
            skArc(sketch, "E284.MirrorCS", {"start": v(-198.58, 45.33) * mm, "mid": v(-206.36, 56.84) * mm, "end": v(-204.43, 70.59) * mm});
            skLineSegment(sketch, "E285.MirrorCS", {"start": v(-145.37, 42.87) * mm, "end": v(-145.37, 19.6) * mm});
            skLineSegment(sketch, "E286.MirrorCS", {"start": v(-64.11, -37.04) * mm, "end": v(-64.11, -8.78) * mm});
            skLineSegment(sketch, "E287.MirrorCS", {"start": v(-193.27, -42.87) * mm, "end": v(-193.27, -19.6) * mm});
            skLineSegment(sketch, "E288.MirrorCS", {"start": v(-71.53, 19.6) * mm, "end": v(-71.53, 35.72) * mm});
            skLineSegment(sketch, "E289.MirrorCS", {"start": v(-96.7, 70.59) * mm, "end": v(-96.7, 36.2) * mm});
            skLineSegment(sketch, "E290.MirrorCS", {"start": v(-235.85, 94.64) * mm, "end": v(-235.62, 31.81) * mm});
            skLineSegment(sketch, "E291.MirrorCS", {"start": v(-203.84, 81.85) * mm, "end": v(-203.84, 94.64) * mm});
            skLineSegment(sketch, "E292.MirrorCS", {"start": v(-58.3, -47.98) * mm, "end": v(-58.3, -3) * mm});
            skLineSegment(sketch, "E293.MirrorCS", {"start": v(-253.6, 3) * mm, "end": v(-280.34, 3) * mm});
            skLineSegment(sketch, "E294.MirrorCS", {"start": v(-83.31, -100.89) * mm, "end": v(-108.08, -100.89) * mm});
            skCircle(sketch, "E295.MirrorC", {"center": v(-151.14, 61.2) * mm, "radius": 10.77 * mm});
            skLineSegment(sketch, "E296.MirrorCS", {"start": v(-134.8, -94.64) * mm, "end": v(-120.6, -94.64) * mm});
            skLineSegment(sketch, "E297.MirrorCS", {"start": v(-126.7, 70.59) * mm, "end": v(-126.7, 36.2) * mm});
            skLineSegment(sketch, "E298.MirrorCS", {"start": v(-83.31, -100.89) * mm, "end": v(-83.31, -75.88) * mm});
            skArc(sketch, "E299.MirrorCS", {"start": v(-230.56, 26.62) * mm, "mid": v(-246.14, 18.77) * mm, "end": v(-253.6, 3) * mm});
            skArc(sketch, "E300.MirrorCS", {"start": v(-211.95, -36.2) * mm, "mid": v(-204.78, -32.32) * mm, "end": v(-198.58, -27.02) * mm});
            skArc(sketch, "E301.MirrorCS", {"start": v(-255.32, -45.33) * mm, "mid": v(-247.54, -56.84) * mm, "end": v(-249.47, -70.59) * mm});
            skArc(sketch, "E302.MirrorCS", {"start": v(-198.58, -45.33) * mm, "mid": v(-206.36, -56.84) * mm, "end": v(-204.43, -70.59) * mm});
            skLineSegment(sketch, "E303.MirrorCS", {"start": v(-241.95, 70.59) * mm, "end": v(-241.95, 36.2) * mm});
            skArc(sketch, "E304.MirrorCS", {"start": v(-140.07, -45.33) * mm, "mid": v(-132.29, -56.84) * mm, "end": v(-134.21, -70.59) * mm});
            skArc(sketch, "E305.MirrorCS", {"start": v(-115.3, -26.62) * mm, "mid": v(-130.89, -18.77) * mm, "end": v(-138.35, -3) * mm});
            skArc(sketch, "E306.MirrorCS", {"start": v(-83.32, -45.33) * mm, "mid": v(-91.1, -56.84) * mm, "end": v(-89.18, -70.59) * mm});
            skLineSegment(sketch, "E307.MirrorCS", {"start": v(-108.08, 26.62) * mm, "end": v(-108.08, 100.89) * mm});
            skLineSegment(sketch, "E308.MirrorCS", {"start": v(-77.54, -79.48) * mm, "end": v(-77.54, -100.89) * mm});
            skLineSegment(sketch, "E309.MirrorCS", {"start": v(-78.02, -42.87) * mm, "end": v(-78.02, -19.6) * mm});
            skCircle(sketch, "E310.MirrorC", {"center": v(-151.14, -61.2) * mm, "radius": 10.77 * mm});
            skLineSegment(sketch, "E311.MirrorCS", {"start": v(-88.58, -94.64) * mm, "end": v(-102.8, -94.64) * mm});
            skArc(sketch, "E312.MirrorCS", {"start": v(-143.44, 8.78) * mm, "mid": v(-134.95, 23.35) * mm, "end": v(-120.36, 31.82) * mm});
            skArc(sketch, "E313.MirrorCS", {"start": v(-143.44, -8.78) * mm, "mid": v(-134.95, -23.35) * mm, "end": v(-120.36, -31.82) * mm});
            skLineSegment(sketch, "E314.MirrorCS", {"start": v(-145.85, -79.48) * mm, "end": v(-145.85, -100.89) * mm});
            skArc(sketch, "E315.MirrorCS", {"start": v(-140.07, 45.33) * mm, "mid": v(-132.29, 56.84) * mm, "end": v(-134.21, 70.59) * mm});
            skLineSegment(sketch, "E316.MirrorCS", {"start": v(-151.86, -19.6) * mm, "end": v(-151.86, -35.72) * mm});
            skLineSegment(sketch, "E317.MirrorCS", {"start": v(-279.38, 75.12) * mm, "end": v(-279.38, 100.89) * mm});
            skLineSegment(sketch, "E318.MirrorCS", {"start": v(-261.1, -79.48) * mm, "end": v(-261.1, -100.89) * mm});
            skArc(sketch, "E319.MirrorCS", {"start": v(-261.1, 79.48) * mm, "mid": v(-270.82, 79.71) * mm, "end": v(-279.38, 75.12) * mm});
            skLineSegment(sketch, "E320.MirrorCS", {"start": v(-195.2, 8.78) * mm, "end": v(-179.37, 8.78) * mm});
            skLineSegment(sketch, "E321.MirrorCS", {"start": v(-120.6, -94.64) * mm, "end": v(-120.36, -31.81) * mm});
            skArc(sketch, "E322.MirrorCS", {"start": v(-261.1, -79.48) * mm, "mid": v(-270.82, -79.71) * mm, "end": v(-279.38, -75.12) * mm});
            skLineSegment(sketch, "E323.MirrorCS", {"start": v(-253.6, -3) * mm, "end": v(-280.34, -3) * mm});
            skLineSegment(sketch, "E324.MirrorCS", {"start": v(-203.84, 94.64) * mm, "end": v(-218.05, 94.64) * mm});
            skArc(sketch, "E325.MirrorCS", {"start": v(-223.34, -26.62) * mm, "mid": v(-207.76, -18.77) * mm, "end": v(-200.3, -3) * mm});
            skLineSegment(sketch, "E326.MirrorCS", {"start": v(-174.52, -75.12) * mm, "end": v(-174.52, -100.89) * mm});
            skLineSegment(sketch, "E327.MirrorCS", {"start": v(-79.94, 8.78) * mm, "end": v(-64.11, 8.78) * mm});
            skLineSegment(sketch, "E328.MirrorCS", {"start": v(-120.6, 94.64) * mm, "end": v(-120.36, 31.81) * mm});
            skLineSegment(sketch, "E329.MirrorCS", {"start": v(-165.09, -47.98) * mm, "end": v(-165.09, -3) * mm});
            skLineSegment(sketch, "E330.MirrorCS", {"start": v(-279.38, -100.89) * mm, "end": v(-261.1, -100.89) * mm});
            skArc(sketch, "E331.MirrorCS", {"start": v(-83.32, 45.33) * mm, "mid": v(-91.1, 56.84) * mm, "end": v(-89.18, 70.59) * mm});
            skLineSegment(sketch, "E332.MirrorCS", {"start": v(-83.31, 100.89) * mm, "end": v(-83.31, 75.88) * mm});
            skLineSegment(sketch, "E333.MirrorCS", {"start": v(-198.57, -100.89) * mm, "end": v(-223.34, -100.89) * mm});
            skLineSegment(sketch, "E334.MirrorCS", {"start": v(-255.32, 27.02) * mm, "end": v(-255.32, 45.33) * mm});
            skArc(sketch, "E335.MirrorCS", {"start": v(-96.7, -36.2) * mm, "mid": v(-89.53, -32.32) * mm, "end": v(-83.32, -27.02) * mm});
            skLineSegment(sketch, "E336.MirrorCS", {"start": v(-77.54, 79.48) * mm, "end": v(-77.54, 100.89) * mm});
            skLineSegment(sketch, "E337.MirrorCS", {"start": v(-126.7, -70.59) * mm, "end": v(-126.7, -36.2) * mm});
            skLineSegment(sketch, "E338.MirrorCS", {"start": v(-198.58, 27.02) * mm, "end": v(-198.58, 45.33) * mm});
            skLineSegment(sketch, "E339.MirrorCS", {"start": v(-250.06, 81.85) * mm, "end": v(-250.06, 94.64) * mm});
            skLineSegment(sketch, "E340.MirrorCS", {"start": v(-79.94, -8.78) * mm, "end": v(-64.11, -8.78) * mm});
            skArc(sketch, "E341.MirrorCS", {"start": v(-165.09, 47.98) * mm, "mid": v(-155.96, 42.6) * mm, "end": v(-145.37, 42.87) * mm});
            skCircle(sketch, "E342.MirrorC", {"center": v(-266.4, 61.2) * mm, "radius": 10.77 * mm});
            skLineSegment(sketch, "E343.MirrorCS", {"start": v(-164.12, 100.89) * mm, "end": v(-145.85, 100.89) * mm});
            skLineSegment(sketch, "E344.MirrorCS", {"start": v(-59.27, -75.12) * mm, "end": v(-59.27, -100.89) * mm});
            skArc(sketch, "E345.MirrorCS", {"start": v(-79.94, -8.78) * mm, "mid": v(-88.44, -23.35) * mm, "end": v(-103.03, -31.82) * mm});
            skArc(sketch, "E346.MirrorCS", {"start": v(-58.3, -47.98) * mm, "mid": v(-67.43, -42.6) * mm, "end": v(-78.02, -42.87) * mm});
            skLineSegment(sketch, "E347.MirrorCS", {"start": v(-83.31, 100.89) * mm, "end": v(-108.08, 100.89) * mm});
            skArc(sketch, "E348.MirrorCS", {"start": v(-165.09, -47.98) * mm, "mid": v(-155.96, -42.6) * mm, "end": v(-145.37, -42.87) * mm});
            skLineSegment(sketch, "E349.MirrorCS", {"start": v(-71.53, -19.6) * mm, "end": v(-71.53, -35.72) * mm});
            skLineSegment(sketch, "E350.MirrorCS", {"start": v(-255.33, 100.89) * mm, "end": v(-255.33, 75.88) * mm});
            skLineSegment(sketch, "E351.MirrorCS", {"start": v(-198.57, 100.89) * mm, "end": v(-198.57, 75.88) * mm});
            skLineSegment(sketch, "E352.MirrorCS", {"start": v(-186.78, 19.6) * mm, "end": v(-186.78, 35.72) * mm});
            skLineSegment(sketch, "E353.MirrorCS", {"start": v(-193.27, 42.87) * mm, "end": v(-193.27, 19.6) * mm});
            skLineSegment(sketch, "E354.MirrorCS", {"start": v(-223.34, 26.62) * mm, "end": v(-223.34, 100.89) * mm});
            skLineSegment(sketch, "E355.MirrorCS", {"start": v(-211.95, -70.59) * mm, "end": v(-211.95, -36.2) * mm});
            skLineSegment(sketch, "E356.MirrorCS", {"start": v(-255.32, -27.02) * mm, "end": v(-255.32, -45.33) * mm});
            skLineSegment(sketch, "E357.MirrorCS", {"start": v(-174.52, -100.89) * mm, "end": v(-192.8, -100.89) * mm});
            skLineSegment(sketch, "E358.MirrorCS", {"start": v(-179.37, 37.04) * mm, "end": v(-179.37, 8.78) * mm});
            skLineSegment(sketch, "E359.MirrorCS", {"start": v(-198.58, -27.02) * mm, "end": v(-198.58, -45.33) * mm});
            skLineSegment(sketch, "E360.MirrorCS", {"start": v(-279.38, -75.12) * mm, "end": v(-279.38, -100.89) * mm});
            skArc(sketch, "E361.MirrorCS", {"start": v(-195.2, -8.78) * mm, "mid": v(-203.69, -23.35) * mm, "end": v(-218.28, -31.82) * mm});
            skArc(sketch, "E362.MirrorCS", {"start": v(-258.7, 8.78) * mm, "mid": v(-250.2, 23.35) * mm, "end": v(-235.62, 31.82) * mm});
            skArc(sketch, "E363.MirrorCS", {"start": v(-223.34, 26.62) * mm, "mid": v(-207.76, 18.77) * mm, "end": v(-200.3, 3) * mm});
            skLineSegment(sketch, "E364.MirrorCS", {"start": v(-279.38, 100.89) * mm, "end": v(-261.1, 100.89) * mm});
            skLineSegment(sketch, "E365.MirrorCS", {"start": v(-274.53, -37.04) * mm, "end": v(-274.53, -8.78) * mm});
            skLineSegment(sketch, "E366.MirrorCS", {"start": v(-169.32, 105.78) * mm, "end": v(-54.07, 105.78) * mm});
            skLineSegment(sketch, "E367.MirrorCS", {"start": v(-169.32, -105.78) * mm, "end": v(-54.07, -105.78) * mm});
            skLineSegment(sketch, "E368.MirrorCS", {"start": v(-195.2, -8.78) * mm, "end": v(-179.37, -8.78) * mm});
            skCircle(sketch, "E369.MirrorC", {"center": v(-226.95, 0) * mm, "radius": 20.2 * mm});
            skCircle(sketch, "E370.MirrorC", {"center": v(-111.7, 0) * mm, "radius": 20.2 * mm});
            skLineSegment(sketch, "E371.MirrorCS", {"start": v(-169.32, 105.78) * mm, "end": v(-284.58, 105.78) * mm});
            skLineSegment(sketch, "E372.MirrorCS", {"start": v(-169.32, -105.78) * mm, "end": v(-284.58, -105.78) * mm});
            skLineSegment(sketch, "E373.MirrorCS", {"start": v(176.44, -105.78) * mm, "end": v(176.44, 105.78) * mm});
            skLineSegment(sketch, "E374.MirrorCS", {"start": v(176.44, 105.78) * mm, "end": v(176.44, -105.78) * mm});
            skLineSegment(sketch, "E375.MirrorCS", {"start": v(406.95, 105.78) * mm, "end": v(406.95, -105.78) * mm});
            skLineSegment(sketch, "E376.MirrorCS", {"start": v(406.95, -105.78) * mm, "end": v(406.95, 105.78) * mm});
            skLineSegment(sketch, "E377.MirrorCS", {"start": v(326.23, -70.59) * mm, "end": v(334.32, -70.59) * mm});
            skLineSegment(sketch, "E378.MirrorCS", {"start": v(334.32, -75.88) * mm, "end": v(334.32, -81.85) * mm});
            skLineSegment(sketch, "E379.MirrorCS", {"start": v(334.32, 75.88) * mm, "end": v(320.94, 75.88) * mm});
            skLineSegment(sketch, "E380.MirrorCS", {"start": v(249.07, 75.88) * mm, "end": v(249.07, 81.85) * mm});
            skLineSegment(sketch, "E381.MirrorCS", {"start": v(372.42, 70.59) * mm, "end": v(364.32, 70.59) * mm});
            skLineSegment(sketch, "E382.MirrorCS", {"start": v(95.72, 70.59) * mm, "end": v(103.81, 70.59) * mm});
            skLineSegment(sketch, "E383.MirrorCS", {"start": v(249.07, -75.88) * mm, "end": v(249.07, -81.85) * mm});
            skLineSegment(sketch, "E384.MirrorCS", {"start": v(364.32, 75.88) * mm, "end": v(364.32, 81.85) * mm});
            skLineSegment(sketch, "E385.MirrorCS", {"start": v(257.16, 70.59) * mm, "end": v(249.07, 70.59) * mm});
            skLineSegment(sketch, "E386.MirrorCS", {"start": v(326.23, 70.59) * mm, "end": v(334.32, 70.59) * mm});
            skLineSegment(sketch, "E387.MirrorCS", {"start": v(326.21, 81.85) * mm, "end": v(334.32, 81.85) * mm});
            skLineSegment(sketch, "E388.MirrorCS", {"start": v(334.32, 75.88) * mm, "end": v(334.32, 81.85) * mm});
            skLineSegment(sketch, "E389.MirrorCS", {"start": v(364.32, -75.88) * mm, "end": v(364.32, -81.85) * mm});
            skLineSegment(sketch, "E390.MirrorCS", {"start": v(372.43, 81.85) * mm, "end": v(364.32, 81.85) * mm});
            skLineSegment(sketch, "E391.MirrorCS", {"start": v(257.18, 81.85) * mm, "end": v(249.07, 81.85) * mm});
            skLineSegment(sketch, "E392.MirrorCS", {"start": v(257.16, -70.59) * mm, "end": v(249.07, -70.59) * mm});
            skLineSegment(sketch, "E393.MirrorCS", {"start": v(219.07, -75.88) * mm, "end": v(219.07, -81.85) * mm});
            skLineSegment(sketch, "E394.MirrorCS", {"start": v(210.98, -70.59) * mm, "end": v(219.07, -70.59) * mm});
            skLineSegment(sketch, "E395.MirrorCS", {"start": v(364.32, 75.88) * mm, "end": v(377.7, 75.88) * mm});
            skLineSegment(sketch, "E396.MirrorCS", {"start": v(103.81, 75.88) * mm, "end": v(103.81, 81.85) * mm});
            skLineSegment(sketch, "E397.MirrorCS", {"start": v(103.81, 75.88) * mm, "end": v(90.43, 75.88) * mm});
            skLineSegment(sketch, "E398.MirrorCS", {"start": v(95.7, 81.85) * mm, "end": v(103.81, 81.85) * mm});
            skLineSegment(sketch, "E399.MirrorCS", {"start": v(249.07, 75.88) * mm, "end": v(262.45, 75.88) * mm});
            skLineSegment(sketch, "E400.MirrorCS", {"start": v(207.42, 3) * mm, "end": v(180.67, 3) * mm});
            skLineSegment(sketch, "E401.MirrorCS", {"start": v(274.24, -19.6) * mm, "end": v(267.75, -19.6) * mm});
            skArc(sketch, "E402.MirrorCS", {"start": v(274.24, -35.72) * mm, "mid": v(278, -36.1) * mm, "end": v(281.65, -37.04) * mm});
            skLineSegment(sketch, "E403.MirrorCS", {"start": v(205.69, 100.89) * mm, "end": v(230.46, 100.89) * mm});
            skLineSegment(sketch, "E404.MirrorCS", {"start": v(205.69, 100.89) * mm, "end": v(205.69, 75.88) * mm});
            skLineSegment(sketch, "E405.MirrorCS", {"start": v(274.24, -19.6) * mm, "end": v(274.24, -35.72) * mm});
            skArc(sketch, "E406.MirrorCS", {"start": v(334.32, -36.2) * mm, "mid": v(327.16, -32.32) * mm, "end": v(320.95, -27.02) * mm});
            skArc(sketch, "E407.MirrorCS", {"start": v(249.07, 36.2) * mm, "mid": v(256.24, 32.32) * mm, "end": v(262.44, 27.02) * mm});
            skLineSegment(sketch, "E408.MirrorCS", {"start": v(95.7, -81.85) * mm, "end": v(95.7, -94.64) * mm});
            skLineSegment(sketch, "E409.MirrorCS", {"start": v(133.82, -75.88) * mm, "end": v(133.82, -81.85) * mm});
            skLineSegment(sketch, "E410.MirrorCS", {"start": v(90.44, 27.02) * mm, "end": v(90.44, 45.33) * mm});
            skLineSegment(sketch, "E411.MirrorCS", {"start": v(95.7, 94.64) * mm, "end": v(109.91, 94.64) * mm});
            skLineSegment(sketch, "E412.MirrorCS", {"start": v(147.19, 27.02) * mm, "end": v(147.19, 45.33) * mm});
            skLineSegment(sketch, "E413.MirrorCS", {"start": v(301.74, -37.04) * mm, "end": v(301.74, -8.78) * mm});
            skLineSegment(sketch, "E414.MirrorCS", {"start": v(260.72, 3) * mm, "end": v(287.46, 3) * mm});
            skArc(sketch, "E415.MirrorCS", {"start": v(287.46, -47.98) * mm, "mid": v(278.34, -42.6) * mm, "end": v(267.75, -42.87) * mm});
            skLineSegment(sketch, "E416.MirrorCS", {"start": v(181.64, 100.89) * mm, "end": v(199.91, 100.89) * mm});
            skArc(sketch, "E417.MirrorCS", {"start": v(402.72, 47.98) * mm, "mid": v(393.6, 42.6) * mm, "end": v(383, 42.87) * mm});
            skLineSegment(sketch, "E418.MirrorCS", {"start": v(133.82, 75.88) * mm, "end": v(147.2, 75.88) * mm});
            skLineSegment(sketch, "E419.MirrorCS", {"start": v(141.93, -94.64) * mm, "end": v(127.72, -94.64) * mm});
            skLineSegment(sketch, "E420.MirrorCS", {"start": v(150.56, 8.78) * mm, "end": v(166.4, 8.78) * mm});
            skArc(sketch, "E421.MirrorCS", {"start": v(133.82, -36.2) * mm, "mid": v(140.98, -32.32) * mm, "end": v(147.19, -27.02) * mm});
            skLineSegment(sketch, "E422.MirrorCS", {"start": v(145.47, 3) * mm, "end": v(172.2, 3) * mm});
            skLineSegment(sketch, "E423.MirrorCS", {"start": v(274.24, 19.6) * mm, "end": v(267.75, 19.6) * mm});
            skLineSegment(sketch, "E424.MirrorCS", {"start": v(265.82, 8.78) * mm, "end": v(281.65, 8.78) * mm});
            skLineSegment(sketch, "E425.MirrorCS", {"start": v(364.32, -75.88) * mm, "end": v(377.7, -75.88) * mm});
            skLineSegment(sketch, "E426.MirrorCS", {"start": v(326.21, 81.85) * mm, "end": v(326.21, 94.64) * mm});
            skLineSegment(sketch, "E427.MirrorCS", {"start": v(377.7, -100.89) * mm, "end": v(377.7, -75.88) * mm});
            skArc(sketch, "E428.MirrorCS", {"start": v(268.22, -79.48) * mm, "mid": v(277.94, -79.71) * mm, "end": v(286.5, -75.12) * mm});
            skLineSegment(sketch, "E429.MirrorCS", {"start": v(207.42, -3) * mm, "end": v(180.67, -3) * mm});
            skLineSegment(sketch, "E430.MirrorCS", {"start": v(186.49, -37.04) * mm, "end": v(186.49, -8.78) * mm});
            skLineSegment(sketch, "E431.MirrorCS", {"start": v(326.21, -94.64) * mm, "end": v(340.42, -94.64) * mm});
            skLineSegment(sketch, "E432.MirrorCS", {"start": v(200.4, 42.87) * mm, "end": v(200.4, 19.6) * mm});
            skLineSegment(sketch, "E433.MirrorCS", {"start": v(322.67, -3) * mm, "end": v(295.93, -3) * mm});
            skLineSegment(sketch, "E434.MirrorCS", {"start": v(193.9, -19.6) * mm, "end": v(193.9, -35.72) * mm});
            skLineSegment(sketch, "E435.MirrorCS", {"start": v(377.7, 27.02) * mm, "end": v(377.7, 45.33) * mm});
            skArc(sketch, "E436.MirrorCS", {"start": v(287.46, 47.98) * mm, "mid": v(278.34, 42.6) * mm, "end": v(267.75, 42.87) * mm});
            skLineSegment(sketch, "E437.MirrorCS", {"start": v(309.16, 19.6) * mm, "end": v(309.16, 35.72) * mm});
            skArc(sketch, "E438.MirrorCS", {"start": v(402.72, -47.98) * mm, "mid": v(393.6, -42.6) * mm, "end": v(383, -42.87) * mm});
            skArc(sketch, "E439.MirrorCS", {"start": v(249.07, -36.2) * mm, "mid": v(256.24, -32.32) * mm, "end": v(262.44, -27.02) * mm});
            skArc(sketch, "E440.MirrorCS", {"start": v(295.93, -47.98) * mm, "mid": v(305.06, -42.6) * mm, "end": v(315.65, -42.87) * mm});
            skLineSegment(sketch, "E441.MirrorCS", {"start": v(383, -42.87) * mm, "end": v(383, -19.6) * mm});
            skArc(sketch, "E442.MirrorCS", {"start": v(158.98, 35.72) * mm, "mid": v(162.74, 36.1) * mm, "end": v(166.4, 37.04) * mm});
            skArc(sketch, "E443.MirrorCS", {"start": v(295.93, 47.98) * mm, "mid": v(305.06, 42.6) * mm, "end": v(315.65, 42.87) * mm});
            skLineSegment(sketch, "E444.MirrorCS", {"start": v(372.43, 81.85) * mm, "end": v(372.43, 94.64) * mm});
            skLineSegment(sketch, "E445.MirrorCS", {"start": v(95.7, 81.85) * mm, "end": v(95.7, 94.64) * mm});
            skLineSegment(sketch, "E446.MirrorCS", {"start": v(267.75, 42.87) * mm, "end": v(267.75, 19.6) * mm});
            skArc(sketch, "E447.MirrorCS", {"start": v(78.65, -35.72) * mm, "mid": v(74.9, -36.1) * mm, "end": v(71.23, -37.04) * mm});
            skLineSegment(sketch, "E448.MirrorCS", {"start": v(90.43, -100.89) * mm, "end": v(90.43, -75.88) * mm});
            skLineSegment(sketch, "E449.MirrorCS", {"start": v(95.7, -81.85) * mm, "end": v(103.81, -81.85) * mm});
            skLineSegment(sketch, "E450.MirrorCS", {"start": v(152.5, -42.87) * mm, "end": v(152.5, -19.6) * mm});
            skLineSegment(sketch, "E451.MirrorCS", {"start": v(103.81, -75.88) * mm, "end": v(103.81, -81.85) * mm});
            skArc(sketch, "E452.MirrorCS", {"start": v(133.82, 36.2) * mm, "mid": v(140.98, 32.32) * mm, "end": v(147.19, 27.02) * mm});
            skLineSegment(sketch, "E453.MirrorCS", {"start": v(90.43, 100.89) * mm, "end": v(115.2, 100.89) * mm});
            skLineSegment(sketch, "E454.MirrorCS", {"start": v(147.2, -100.89) * mm, "end": v(147.2, -75.88) * mm});
            skLineSegment(sketch, "E455.MirrorCS", {"start": v(66.39, -100.89) * mm, "end": v(84.66, -100.89) * mm});
            skLineSegment(sketch, "E456.MirrorCS", {"start": v(171.24, -100.89) * mm, "end": v(152.97, -100.89) * mm});
            skLineSegment(sketch, "E457.MirrorCS", {"start": v(326.21, -81.85) * mm, "end": v(334.32, -81.85) * mm});
            skArc(sketch, "E458.MirrorCS", {"start": v(309.16, 35.72) * mm, "mid": v(305.4, 36.1) * mm, "end": v(301.74, 37.04) * mm});
            skArc(sketch, "E459.MirrorCS", {"start": v(389.5, -35.72) * mm, "mid": v(393.25, -36.1) * mm, "end": v(396.9, -37.04) * mm});
            skArc(sketch, "E460.MirrorCS", {"start": v(364.32, 36.2) * mm, "mid": v(371.5, 32.32) * mm, "end": v(377.7, 27.02) * mm});
            skLineSegment(sketch, "E461.MirrorCS", {"start": v(375.98, 3) * mm, "end": v(402.72, 3) * mm});
            skLineSegment(sketch, "E462.MirrorCS", {"start": v(372.43, -94.64) * mm, "end": v(358.23, -94.64) * mm});
            skArc(sketch, "E463.MirrorCS", {"start": v(199.91, 79.48) * mm, "mid": v(190.2, 79.71) * mm, "end": v(181.64, 75.12) * mm});
            skLineSegment(sketch, "E464.MirrorCS", {"start": v(286.5, -100.89) * mm, "end": v(268.22, -100.89) * mm});
            skLineSegment(sketch, "E465.MirrorCS", {"start": v(389.5, 19.6) * mm, "end": v(389.5, 35.72) * mm});
            skLineSegment(sketch, "E466.MirrorCS", {"start": v(381.07, -8.78) * mm, "end": v(396.9, -8.78) * mm});
            skLineSegment(sketch, "E467.MirrorCS", {"start": v(205.7, -27.02) * mm, "end": v(205.7, -45.33) * mm});
            skLineSegment(sketch, "E468.MirrorCS", {"start": v(315.65, 42.87) * mm, "end": v(315.65, 19.6) * mm});
            skLineSegment(sketch, "E469.MirrorCS", {"start": v(103.81, -75.88) * mm, "end": v(90.43, -75.88) * mm});
            skLineSegment(sketch, "E470.MirrorCS", {"start": v(202.32, 8.78) * mm, "end": v(186.49, 8.78) * mm});
            skLineSegment(sketch, "E471.MirrorCS", {"start": v(210.96, -94.64) * mm, "end": v(225.17, -94.64) * mm});
            skLineSegment(sketch, "E472.MirrorCS", {"start": v(133.82, 75.88) * mm, "end": v(133.82, 81.85) * mm});
            skArc(sketch, "E473.MirrorCS", {"start": v(103.81, 36.2) * mm, "mid": v(96.65, 32.32) * mm, "end": v(90.44, 27.02) * mm});
            skArc(sketch, "E474.MirrorCS", {"start": v(180.67, -47.98) * mm, "mid": v(189.8, -42.6) * mm, "end": v(200.4, -42.87) * mm});
            skLineSegment(sketch, "E475.MirrorCS", {"start": v(257.18, 81.85) * mm, "end": v(257.18, 94.64) * mm});
            skLineSegment(sketch, "E476.MirrorCS", {"start": v(377.7, -27.02) * mm, "end": v(377.7, -45.33) * mm});
            skLineSegment(sketch, "E477.MirrorCS", {"start": v(381.07, 8.78) * mm, "end": v(396.9, 8.78) * mm});
            skArc(sketch, "E478.MirrorCS", {"start": v(103.81, -36.2) * mm, "mid": v(96.65, -32.32) * mm, "end": v(90.44, -27.02) * mm});
            skArc(sketch, "E479.MirrorCS", {"start": v(152.97, -79.48) * mm, "mid": v(162.68, -79.71) * mm, "end": v(171.24, -75.12) * mm});
            skLineSegment(sketch, "E480.MirrorCS", {"start": v(267.75, -42.87) * mm, "end": v(267.75, -19.6) * mm});
            skLineSegment(sketch, "E481.MirrorCS", {"start": v(389.5, -19.6) * mm, "end": v(383, -19.6) * mm});
            skLineSegment(sketch, "E482.MirrorCS", {"start": v(389.5, 19.6) * mm, "end": v(383, 19.6) * mm});
            skLineSegment(sketch, "E483.MirrorCS", {"start": v(257.18, -81.85) * mm, "end": v(249.07, -81.85) * mm});
            skLineSegment(sketch, "E484.MirrorCS", {"start": v(171.24, 100.89) * mm, "end": v(152.97, 100.89) * mm});
            skLineSegment(sketch, "E485.MirrorCS", {"start": v(133.82, -75.88) * mm, "end": v(147.2, -75.88) * mm});
            skLineSegment(sketch, "E486.MirrorCS", {"start": v(141.9, -70.59) * mm, "end": v(133.82, -70.59) * mm});
            skLineSegment(sketch, "E487.MirrorCS", {"start": v(145.47, -3) * mm, "end": v(172.2, -3) * mm});
            skLineSegment(sketch, "E488.MirrorCS", {"start": v(87.06, -8.78) * mm, "end": v(71.23, -8.78) * mm});
            skLineSegment(sketch, "E489.MirrorCS", {"start": v(158.98, -19.6) * mm, "end": v(152.5, -19.6) * mm});
            skLineSegment(sketch, "E490.MirrorCS", {"start": v(95.7, -94.64) * mm, "end": v(109.91, -94.64) * mm});
            skLineSegment(sketch, "E491.MirrorCS", {"start": v(320.94, 100.89) * mm, "end": v(320.94, 75.88) * mm});
            skArc(sketch, "E492.MirrorCS", {"start": v(334.32, 36.2) * mm, "mid": v(327.16, 32.32) * mm, "end": v(320.95, 27.02) * mm});
            skLineSegment(sketch, "E493.MirrorCS", {"start": v(166.4, -37.04) * mm, "end": v(166.4, -8.78) * mm});
            skLineSegment(sketch, "E494.MirrorCS", {"start": v(92.16, 3) * mm, "end": v(65.42, 3) * mm});
            skLineSegment(sketch, "E495.MirrorCS", {"start": v(90.44, -27.02) * mm, "end": v(90.44, -45.33) * mm});
            skLineSegment(sketch, "E496.MirrorCS", {"start": v(85.14, -42.87) * mm, "end": v(85.14, -19.6) * mm});
            skLineSegment(sketch, "E497.MirrorCS", {"start": v(219.07, 75.88) * mm, "end": v(219.07, 81.85) * mm});
            skLineSegment(sketch, "E498.MirrorCS", {"start": v(262.45, 100.89) * mm, "end": v(237.68, 100.89) * mm});
            skLineSegment(sketch, "E499.MirrorCS", {"start": v(205.7, 27.02) * mm, "end": v(205.7, 45.33) * mm});
            skLineSegment(sketch, "E500.MirrorCS", {"start": v(85.14, 42.87) * mm, "end": v(85.14, 19.6) * mm});
            skLineSegment(sketch, "E501.MirrorCS", {"start": v(219.07, 75.88) * mm, "end": v(205.69, 75.88) * mm});
            skLineSegment(sketch, "E502.MirrorCS", {"start": v(309.16, -19.6) * mm, "end": v(315.65, -19.6) * mm});
            skLineSegment(sketch, "E503.MirrorCS", {"start": v(78.65, -19.6) * mm, "end": v(85.14, -19.6) * mm});
            skArc(sketch, "E504.MirrorCS", {"start": v(172.2, 47.98) * mm, "mid": v(163.08, 42.6) * mm, "end": v(152.5, 42.87) * mm});
            skArc(sketch, "E505.MirrorCS", {"start": v(193.9, 35.72) * mm, "mid": v(190.15, 36.1) * mm, "end": v(186.49, 37.04) * mm});
            skLineSegment(sketch, "E506.MirrorCS", {"start": v(210.96, -81.85) * mm, "end": v(219.07, -81.85) * mm});
            skLineSegment(sketch, "E507.MirrorCS", {"start": v(377.7, 100.89) * mm, "end": v(352.94, 100.89) * mm});
            skLineSegment(sketch, "E508.MirrorCS", {"start": v(309.16, 19.6) * mm, "end": v(315.65, 19.6) * mm});
            skLineSegment(sketch, "E509.MirrorCS", {"start": v(372.43, -81.85) * mm, "end": v(364.32, -81.85) * mm});
            skLineSegment(sketch, "E510.MirrorCS", {"start": v(383, 42.87) * mm, "end": v(383, 19.6) * mm});
            skLineSegment(sketch, "E511.MirrorCS", {"start": v(326.21, 94.64) * mm, "end": v(340.42, 94.64) * mm});
            skArc(sketch, "E512.MirrorCS", {"start": v(309.16, -35.72) * mm, "mid": v(305.4, -36.1) * mm, "end": v(301.74, -37.04) * mm});
            skLineSegment(sketch, "E513.MirrorCS", {"start": v(326.21, -81.85) * mm, "end": v(326.21, -94.64) * mm});
            skArc(sketch, "E514.MirrorCS", {"start": v(199.91, -79.48) * mm, "mid": v(190.2, -79.71) * mm, "end": v(181.64, -75.12) * mm});
            skLineSegment(sketch, "E515.MirrorCS", {"start": v(141.93, -81.85) * mm, "end": v(133.82, -81.85) * mm});
            skLineSegment(sketch, "E516.MirrorCS", {"start": v(158.98, 19.6) * mm, "end": v(158.98, 35.72) * mm});
            skLineSegment(sketch, "E517.MirrorCS", {"start": v(95.72, -70.59) * mm, "end": v(103.81, -70.59) * mm});
            skLineSegment(sketch, "E518.MirrorCS", {"start": v(274.24, 19.6) * mm, "end": v(274.24, 35.72) * mm});
            skLineSegment(sketch, "E519.MirrorCS", {"start": v(286.5, 100.89) * mm, "end": v(268.22, 100.89) * mm});
            skLineSegment(sketch, "E520.MirrorCS", {"start": v(257.18, -94.64) * mm, "end": v(242.97, -94.64) * mm});
            skArc(sketch, "E521.MirrorCS", {"start": v(364.32, -36.2) * mm, "mid": v(371.5, -32.32) * mm, "end": v(377.7, -27.02) * mm});
            skLineSegment(sketch, "E522.MirrorCS", {"start": v(181.64, -100.89) * mm, "end": v(199.91, -100.89) * mm});
            skLineSegment(sketch, "E523.MirrorCS", {"start": v(262.45, -100.89) * mm, "end": v(262.45, -75.88) * mm});
            skLineSegment(sketch, "E524.MirrorCS", {"start": v(309.16, -19.6) * mm, "end": v(309.16, -35.72) * mm});
            skArc(sketch, "E525.MirrorCS", {"start": v(389.5, 35.72) * mm, "mid": v(393.25, 36.1) * mm, "end": v(396.9, 37.04) * mm});
            skLineSegment(sketch, "E526.MirrorCS", {"start": v(375.98, -3) * mm, "end": v(402.72, -3) * mm});
            skLineSegment(sketch, "E527.MirrorCS", {"start": v(265.82, -8.78) * mm, "end": v(281.65, -8.78) * mm});
            skArc(sketch, "E528.MirrorCS", {"start": v(180.67, 47.98) * mm, "mid": v(189.8, 42.6) * mm, "end": v(200.4, 42.87) * mm});
            skArc(sketch, "E529.MirrorCS", {"start": v(152.97, 79.48) * mm, "mid": v(162.68, 79.71) * mm, "end": v(171.24, 75.12) * mm});
            skLineSegment(sketch, "E530.MirrorCS", {"start": v(141.9, 70.59) * mm, "end": v(133.82, 70.59) * mm});
            skLineSegment(sketch, "E531.MirrorCS", {"start": v(141.93, 81.85) * mm, "end": v(141.93, 94.64) * mm});
            skArc(sketch, "E532.MirrorCS", {"start": v(158.98, -35.72) * mm, "mid": v(162.74, -36.1) * mm, "end": v(166.4, -37.04) * mm});
            skArc(sketch, "E533.MirrorCS", {"start": v(84.66, -79.48) * mm, "mid": v(74.95, -79.71) * mm, "end": v(66.39, -75.12) * mm});
            skLineSegment(sketch, "E534.MirrorCS", {"start": v(372.42, -70.59) * mm, "end": v(364.32, -70.59) * mm});
            skLineSegment(sketch, "E535.MirrorCS", {"start": v(152.5, 42.87) * mm, "end": v(152.5, 19.6) * mm});
            skArc(sketch, "E536.MirrorCS", {"start": v(84.66, 79.48) * mm, "mid": v(74.95, 79.71) * mm, "end": v(66.39, 75.12) * mm});
            skLineSegment(sketch, "E537.MirrorCS", {"start": v(166.4, 37.04) * mm, "end": v(166.4, 8.78) * mm});
            skLineSegment(sketch, "E538.MirrorCS", {"start": v(317.57, -8.78) * mm, "end": v(301.74, -8.78) * mm});
            skLineSegment(sketch, "E539.MirrorCS", {"start": v(202.32, -8.78) * mm, "end": v(186.49, -8.78) * mm});
            skLineSegment(sketch, "E540.MirrorCS", {"start": v(92.16, -3) * mm, "end": v(65.42, -3) * mm});
            skLineSegment(sketch, "E541.MirrorCS", {"start": v(193.9, -19.6) * mm, "end": v(200.4, -19.6) * mm});
            skLineSegment(sketch, "E542.MirrorCS", {"start": v(219.07, -75.88) * mm, "end": v(205.69, -75.88) * mm});
            skLineSegment(sketch, "E543.MirrorCS", {"start": v(210.96, 94.64) * mm, "end": v(225.17, 94.64) * mm});
            skLineSegment(sketch, "E544.MirrorCS", {"start": v(210.98, 70.59) * mm, "end": v(219.07, 70.59) * mm});
            skLineSegment(sketch, "E545.MirrorCS", {"start": v(210.96, 81.85) * mm, "end": v(210.96, 94.64) * mm});
            skLineSegment(sketch, "E546.MirrorCS", {"start": v(87.06, 8.78) * mm, "end": v(71.23, 8.78) * mm});
            skLineSegment(sketch, "E547.MirrorCS", {"start": v(301.74, 37.04) * mm, "end": v(301.74, 8.78) * mm});
            skLineSegment(sketch, "E548.MirrorCS", {"start": v(158.98, -19.6) * mm, "end": v(158.98, -35.72) * mm});
            skLineSegment(sketch, "E549.MirrorCS", {"start": v(320.95, 27.02) * mm, "end": v(320.95, 45.33) * mm});
            skLineSegment(sketch, "E550.MirrorCS", {"start": v(193.9, 19.6) * mm, "end": v(193.9, 35.72) * mm});
            skLineSegment(sketch, "E551.MirrorCS", {"start": v(193.9, 19.6) * mm, "end": v(200.4, 19.6) * mm});
            skArc(sketch, "E552.MirrorCS", {"start": v(219.07, -36.2) * mm, "mid": v(211.9, -32.32) * mm, "end": v(205.7, -27.02) * mm});
            skLineSegment(sketch, "E553.MirrorCS", {"start": v(150.56, -8.78) * mm, "end": v(166.4, -8.78) * mm});
            skLineSegment(sketch, "E554.MirrorCS", {"start": v(141.93, 94.64) * mm, "end": v(127.72, 94.64) * mm});
            skLineSegment(sketch, "E555.MirrorCS", {"start": v(249.07, -75.88) * mm, "end": v(262.45, -75.88) * mm});
            skLineSegment(sketch, "E556.MirrorCS", {"start": v(320.94, -100.89) * mm, "end": v(320.94, -75.88) * mm});
            skLineSegment(sketch, "E557.MirrorCS", {"start": v(78.65, -19.6) * mm, "end": v(78.65, -35.72) * mm});
            skLineSegment(sketch, "E558.MirrorCS", {"start": v(262.44, -27.02) * mm, "end": v(262.44, -45.33) * mm});
            skLineSegment(sketch, "E559.MirrorCS", {"start": v(315.65, -42.87) * mm, "end": v(315.65, -19.6) * mm});
            skArc(sketch, "E560.MirrorCS", {"start": v(219.07, 36.2) * mm, "mid": v(211.9, 32.32) * mm, "end": v(205.7, 27.02) * mm});
            skLineSegment(sketch, "E561.MirrorCS", {"start": v(320.95, -27.02) * mm, "end": v(320.95, -45.33) * mm});
            skLineSegment(sketch, "E562.MirrorCS", {"start": v(200.4, -42.87) * mm, "end": v(200.4, -19.6) * mm});
            skLineSegment(sketch, "E563.MirrorCS", {"start": v(372.43, -81.85) * mm, "end": v(372.43, -94.64) * mm});
            skLineSegment(sketch, "E564.MirrorCS", {"start": v(377.7, 100.89) * mm, "end": v(377.7, 75.88) * mm});
            skLineSegment(sketch, "E565.MirrorCS", {"start": v(317.57, 8.78) * mm, "end": v(301.74, 8.78) * mm});
            skArc(sketch, "E566.MirrorCS", {"start": v(274.24, 35.72) * mm, "mid": v(278, 36.1) * mm, "end": v(281.65, 37.04) * mm});
            skLineSegment(sketch, "E567.MirrorCS", {"start": v(186.49, 37.04) * mm, "end": v(186.49, 8.78) * mm});
            skLineSegment(sketch, "E568.MirrorCS", {"start": v(262.44, 27.02) * mm, "end": v(262.44, 45.33) * mm});
            skLineSegment(sketch, "E569.MirrorCS", {"start": v(262.45, 100.89) * mm, "end": v(262.45, 75.88) * mm});
            skLineSegment(sketch, "E570.MirrorCS", {"start": v(320.94, 100.89) * mm, "end": v(345.71, 100.89) * mm});
            skLineSegment(sketch, "E571.MirrorCS", {"start": v(260.72, -3) * mm, "end": v(287.46, -3) * mm});
            skLineSegment(sketch, "E572.MirrorCS", {"start": v(141.93, 81.85) * mm, "end": v(133.82, 81.85) * mm});
            skLineSegment(sketch, "E573.MirrorCS", {"start": v(389.5, -19.6) * mm, "end": v(389.5, -35.72) * mm});
            skLineSegment(sketch, "E574.MirrorCS", {"start": v(78.65, 19.6) * mm, "end": v(85.14, 19.6) * mm});
            skLineSegment(sketch, "E575.MirrorCS", {"start": v(322.67, 3) * mm, "end": v(295.93, 3) * mm});
            skLineSegment(sketch, "E576.MirrorCS", {"start": v(257.18, 94.64) * mm, "end": v(242.97, 94.64) * mm});
            skLineSegment(sketch, "E577.MirrorCS", {"start": v(205.69, -100.89) * mm, "end": v(205.69, -75.88) * mm});
            skLineSegment(sketch, "E578.MirrorCS", {"start": v(141.93, -81.85) * mm, "end": v(141.93, -94.64) * mm});
            skLineSegment(sketch, "E579.MirrorCS", {"start": v(90.43, 100.89) * mm, "end": v(90.43, 75.88) * mm});
            skLineSegment(sketch, "E580.MirrorCS", {"start": v(158.98, 19.6) * mm, "end": v(152.5, 19.6) * mm});
            skLineSegment(sketch, "E581.MirrorCS", {"start": v(257.18, -81.85) * mm, "end": v(257.18, -94.64) * mm});
            skLineSegment(sketch, "E582.MirrorCS", {"start": v(147.2, 100.89) * mm, "end": v(147.2, 75.88) * mm});
            skArc(sketch, "E583.MirrorCS", {"start": v(78.65, 35.72) * mm, "mid": v(74.9, 36.1) * mm, "end": v(71.23, 37.04) * mm});
            skLineSegment(sketch, "E584.MirrorCS", {"start": v(66.39, 100.89) * mm, "end": v(84.66, 100.89) * mm});
            skLineSegment(sketch, "E585.MirrorCS", {"start": v(147.19, -27.02) * mm, "end": v(147.19, -45.33) * mm});
            skLineSegment(sketch, "E586.MirrorCS", {"start": v(372.43, 94.64) * mm, "end": v(358.23, 94.64) * mm});
            skLineSegment(sketch, "E587.MirrorCS", {"start": v(334.32, -75.88) * mm, "end": v(320.94, -75.88) * mm});
            skArc(sketch, "E588.MirrorCS", {"start": v(65.42, 47.98) * mm, "mid": v(74.55, 42.6) * mm, "end": v(85.14, 42.87) * mm});
            skArc(sketch, "E589.MirrorCS", {"start": v(65.42, -47.98) * mm, "mid": v(74.55, -42.6) * mm, "end": v(85.14, -42.87) * mm});
            skLineSegment(sketch, "E590.MirrorCS", {"start": v(147.2, 100.89) * mm, "end": v(122.43, 100.89) * mm});
            skLineSegment(sketch, "E591.MirrorCS", {"start": v(78.65, 19.6) * mm, "end": v(78.65, 35.72) * mm});
            skLineSegment(sketch, "E592.MirrorCS", {"start": v(210.96, 81.85) * mm, "end": v(219.07, 81.85) * mm});
            skArc(sketch, "E593.MirrorCS", {"start": v(172.2, -47.98) * mm, "mid": v(163.08, -42.6) * mm, "end": v(152.5, -42.87) * mm});
            skArc(sketch, "E594.MirrorCS", {"start": v(268.22, 79.48) * mm, "mid": v(277.94, 79.71) * mm, "end": v(286.5, 75.12) * mm});
            skArc(sketch, "E595.MirrorCS", {"start": v(193.9, -35.72) * mm, "mid": v(190.15, -36.1) * mm, "end": v(186.49, -37.04) * mm});
            skLineSegment(sketch, "E596.MirrorCS", {"start": v(210.96, -81.85) * mm, "end": v(210.96, -94.64) * mm});
            skLineSegment(sketch, "E597.MirrorCS", {"start": v(205.69, -100.89) * mm, "end": v(230.46, -100.89) * mm});
            skLineSegment(sketch, "E598.MirrorCS", {"start": v(90.43, -100.89) * mm, "end": v(115.2, -100.89) * mm});
            skLineSegment(sketch, "E599.MirrorCS", {"start": v(262.45, -100.89) * mm, "end": v(237.68, -100.89) * mm});
            skArc(sketch, "E600.MirrorCS", {"start": v(230.46, 26.62) * mm, "mid": v(214.88, 18.77) * mm, "end": v(207.42, 3) * mm});
            skLineSegment(sketch, "E601.MirrorCS", {"start": v(147.2, -100.89) * mm, "end": v(122.43, -100.89) * mm});
            skLineSegment(sketch, "E602.MirrorCS", {"start": v(296.9, 75.12) * mm, "end": v(296.9, 100.89) * mm});
            skArc(sketch, "E603.MirrorCS", {"start": v(377.7, 45.33) * mm, "mid": v(369.92, 56.84) * mm, "end": v(371.84, 70.59) * mm});
            skLineSegment(sketch, "E604.MirrorCS", {"start": v(377.7, -100.89) * mm, "end": v(352.94, -100.89) * mm});
            skArc(sketch, "E605.MirrorCS", {"start": v(317.57, 8.78) * mm, "mid": v(326.06, 23.35) * mm, "end": v(340.66, 31.82) * mm});
            skArc(sketch, "E606.MirrorCS", {"start": v(317.57, -8.78) * mm, "mid": v(326.06, -23.35) * mm, "end": v(340.66, -31.82) * mm});
            skLineSegment(sketch, "E607.MirrorCS", {"start": v(383.48, 79.48) * mm, "end": v(383.48, 100.89) * mm});
            skLineSegment(sketch, "E608.MirrorCS", {"start": v(402.72, 47.98) * mm, "end": v(402.72, 3) * mm});
            skLineSegment(sketch, "E609.MirrorCS", {"start": v(171.24, 75.12) * mm, "end": v(171.24, 100.89) * mm});
            skArc(sketch, "E610.MirrorCS", {"start": v(115.2, 26.62) * mm, "mid": v(99.62, 18.77) * mm, "end": v(92.16, 3) * mm});
            skArc(sketch, "E611.MirrorCS", {"start": v(122.43, -26.62) * mm, "mid": v(138, -18.77) * mm, "end": v(145.47, -3) * mm});
            skArc(sketch, "E612.MirrorCS", {"start": v(205.7, -45.33) * mm, "mid": v(213.48, -56.84) * mm, "end": v(211.55, -70.59) * mm});
            skLineSegment(sketch, "E613.MirrorCS", {"start": v(340.42, 94.64) * mm, "end": v(340.66, 31.81) * mm});
            skLineSegment(sketch, "E614.MirrorCS", {"start": v(345.71, -26.62) * mm, "end": v(345.71, -100.89) * mm});
            skCircle(sketch, "E615.MirrorC", {"center": v(309.88, -61.2) * mm, "radius": 10.77 * mm});
            skLineSegment(sketch, "E616.MirrorCS", {"start": v(320.94, -100.89) * mm, "end": v(345.71, -100.89) * mm});
            skLineSegment(sketch, "E617.MirrorCS", {"start": v(401.75, 75.12) * mm, "end": v(401.75, 100.89) * mm});
            skLineSegment(sketch, "E618.MirrorCS", {"start": v(345.71, 26.62) * mm, "end": v(345.71, 100.89) * mm});
            skArc(sketch, "E619.MirrorCS", {"start": v(381.07, 8.78) * mm, "mid": v(372.58, 23.35) * mm, "end": v(358, 31.82) * mm});
            skArc(sketch, "E620.MirrorCS", {"start": v(383.48, -79.48) * mm, "mid": v(393.2, -79.71) * mm, "end": v(401.75, -75.12) * mm});
            skArc(sketch, "E621.MirrorCS", {"start": v(87.06, -8.78) * mm, "mid": v(95.56, -23.35) * mm, "end": v(110.15, -31.82) * mm});
            skLineSegment(sketch, "E622.MirrorCS", {"start": v(65.42, -47.98) * mm, "end": v(65.42, -3) * mm});
            skCircle(sketch, "E623.MirrorC", {"center": v(309.88, 61.2) * mm, "radius": 10.77 * mm});
            skCircle(sketch, "E624.MirrorC", {"center": v(194.62, -61.2) * mm, "radius": 10.77 * mm});
            skLineSegment(sketch, "E625.MirrorCS", {"start": v(315.17, 79.48) * mm, "end": v(315.17, 100.89) * mm});
            skLineSegment(sketch, "E626.MirrorCS", {"start": v(296.9, -75.12) * mm, "end": v(296.9, -100.89) * mm});
            skArc(sketch, "E627.MirrorCS", {"start": v(320.95, -45.33) * mm, "mid": v(328.73, -56.84) * mm, "end": v(326.8, -70.59) * mm});
            skCircle(sketch, "E628.MirrorC", {"center": v(273.52, -61.2) * mm, "radius": 10.77 * mm});
            skArc(sketch, "E629.MirrorCS", {"start": v(345.71, 26.62) * mm, "mid": v(330.13, 18.77) * mm, "end": v(322.67, 3) * mm});
            skLineSegment(sketch, "E630.MirrorCS", {"start": v(268.22, 79.48) * mm, "end": v(268.22, 100.89) * mm});
            skLineSegment(sketch, "E631.MirrorCS", {"start": v(249.07, 70.59) * mm, "end": v(249.07, 36.2) * mm});
            skLineSegment(sketch, "E632.MirrorCS", {"start": v(281.65, 37.04) * mm, "end": v(281.65, 8.78) * mm});
            skLineSegment(sketch, "E633.MirrorCS", {"start": v(334.32, -70.59) * mm, "end": v(334.32, -36.2) * mm});
            skLineSegment(sketch, "E634.MirrorCS", {"start": v(315.17, -79.48) * mm, "end": v(315.17, -100.89) * mm});
            skLineSegment(sketch, "E635.MirrorCS", {"start": v(396.9, -37.04) * mm, "end": v(396.9, -8.78) * mm});
            skArc(sketch, "E636.MirrorCS", {"start": v(230.46, -26.62) * mm, "mid": v(214.88, -18.77) * mm, "end": v(207.42, -3) * mm});
            skLineSegment(sketch, "E637.MirrorCS", {"start": v(402.72, -47.98) * mm, "end": v(402.72, -3) * mm});
            skCircle(sketch, "E638.MirrorC", {"center": v(273.52, 61.2) * mm, "radius": 10.77 * mm});
            skLineSegment(sketch, "E639.MirrorCS", {"start": v(84.66, 79.48) * mm, "end": v(84.66, 100.89) * mm});
            skLineSegment(sketch, "E640.MirrorCS", {"start": v(127.72, 94.64) * mm, "end": v(127.48, 31.81) * mm});
            skCircle(sketch, "E641.MirrorC", {"center": v(158.26, 61.2) * mm, "radius": 10.77 * mm});
            skLineSegment(sketch, "E642.MirrorCS", {"start": v(115.2, -26.62) * mm, "end": v(115.2, -100.89) * mm});
            skLineSegment(sketch, "E643.MirrorCS", {"start": v(103.81, 70.59) * mm, "end": v(103.81, 36.2) * mm});
            skCircle(sketch, "E644.MirrorC", {"center": v(79.37, 61.2) * mm, "radius": 10.77 * mm});
            skLineSegment(sketch, "E645.MirrorCS", {"start": v(364.32, -70.59) * mm, "end": v(364.32, -36.2) * mm});
            skLineSegment(sketch, "E646.MirrorCS", {"start": v(286.5, -75.12) * mm, "end": v(286.5, -100.89) * mm});
            skLineSegment(sketch, "E647.MirrorCS", {"start": v(401.75, 100.89) * mm, "end": v(383.48, 100.89) * mm});
            skLineSegment(sketch, "E648.MirrorCS", {"start": v(352.94, 26.62) * mm, "end": v(352.94, 100.89) * mm});
            skLineSegment(sketch, "E649.MirrorCS", {"start": v(396.9, 37.04) * mm, "end": v(396.9, 8.78) * mm});
            skLineSegment(sketch, "E650.MirrorCS", {"start": v(340.42, -94.64) * mm, "end": v(340.66, -31.81) * mm});
            skCircle(sketch, "E651.MirrorC", {"center": v(388.77, 61.2) * mm, "radius": 10.77 * mm});
            skLineSegment(sketch, "E652.MirrorCS", {"start": v(358.23, -94.64) * mm, "end": v(358, -31.81) * mm});
            skLineSegment(sketch, "E653.MirrorCS", {"start": v(71.23, -37.04) * mm, "end": v(71.23, -8.78) * mm});
            skArc(sketch, "E654.MirrorCS", {"start": v(315.17, 79.48) * mm, "mid": v(305.46, 79.71) * mm, "end": v(296.9, 75.12) * mm});
            skLineSegment(sketch, "E655.MirrorCS", {"start": v(225.17, 94.64) * mm, "end": v(225.4, 31.81) * mm});
            skLineSegment(sketch, "E656.MirrorCS", {"start": v(268.22, -79.48) * mm, "end": v(268.22, -100.89) * mm});
            skLineSegment(sketch, "E657.MirrorCS", {"start": v(383.48, -79.48) * mm, "end": v(383.48, -100.89) * mm});
            skLineSegment(sketch, "E658.MirrorCS", {"start": v(281.65, -37.04) * mm, "end": v(281.65, -8.78) * mm});
            skLineSegment(sketch, "E659.MirrorCS", {"start": v(230.46, -26.62) * mm, "end": v(230.46, -100.89) * mm});
            skArc(sketch, "E660.MirrorCS", {"start": v(352.94, -26.62) * mm, "mid": v(368.52, -18.77) * mm, "end": v(375.98, -3) * mm});
            skArc(sketch, "E661.MirrorCS", {"start": v(122.43, 26.62) * mm, "mid": v(138, 18.77) * mm, "end": v(145.47, 3) * mm});
            skLineSegment(sketch, "E662.MirrorCS", {"start": v(152.97, -79.48) * mm, "end": v(152.97, -100.89) * mm});
            skLineSegment(sketch, "E663.MirrorCS", {"start": v(109.91, -94.64) * mm, "end": v(110.15, -31.81) * mm});
            skLineSegment(sketch, "E664.MirrorCS", {"start": v(71.23, 37.04) * mm, "end": v(71.23, 8.78) * mm});
            skLineSegment(sketch, "E665.MirrorCS", {"start": v(122.43, 26.62) * mm, "end": v(122.43, 100.89) * mm});
            skArc(sketch, "E666.MirrorCS", {"start": v(147.19, -45.33) * mm, "mid": v(139.4, -56.84) * mm, "end": v(141.33, -70.59) * mm});
            skLineSegment(sketch, "E667.MirrorCS", {"start": v(199.91, 79.48) * mm, "end": v(199.91, 100.89) * mm});
            skLineSegment(sketch, "E668.MirrorCS", {"start": v(180.67, -47.98) * mm, "end": v(180.67, -3) * mm});
            skArc(sketch, "E669.MirrorCS", {"start": v(262.44, -45.33) * mm, "mid": v(254.66, -56.84) * mm, "end": v(256.59, -70.59) * mm});
            skCircle(sketch, "E670.MirrorC", {"center": v(194.62, 61.2) * mm, "radius": 10.77 * mm});
            skLineSegment(sketch, "E671.MirrorCS", {"start": v(352.94, -26.62) * mm, "end": v(352.94, -100.89) * mm});
            skCircle(sketch, "E672.MirrorC", {"center": v(158.26, -61.2) * mm, "radius": 10.77 * mm});
            skLineSegment(sketch, "E673.MirrorCS", {"start": v(66.39, -75.12) * mm, "end": v(66.39, -100.89) * mm});
            skLineSegment(sketch, "E674.MirrorCS", {"start": v(237.68, 26.62) * mm, "end": v(237.68, 100.89) * mm});
            skLineSegment(sketch, "E675.MirrorCS", {"start": v(115.2, 26.62) * mm, "end": v(115.2, 100.89) * mm});
            skLineSegment(sketch, "E676.MirrorCS", {"start": v(225.17, -94.64) * mm, "end": v(225.4, -31.81) * mm});
            skLineSegment(sketch, "E677.MirrorCS", {"start": v(249.07, -70.59) * mm, "end": v(249.07, -36.2) * mm});
            skArc(sketch, "E678.MirrorCS", {"start": v(237.68, -26.62) * mm, "mid": v(253.26, -18.77) * mm, "end": v(260.72, -3) * mm});
            skLineSegment(sketch, "E679.MirrorCS", {"start": v(219.07, 70.59) * mm, "end": v(219.07, 36.2) * mm});
            skArc(sketch, "E680.MirrorCS", {"start": v(147.19, 45.33) * mm, "mid": v(139.4, 56.84) * mm, "end": v(141.33, 70.59) * mm});
            skArc(sketch, "E681.MirrorCS", {"start": v(315.17, -79.48) * mm, "mid": v(305.46, -79.71) * mm, "end": v(296.9, -75.12) * mm});
            skLineSegment(sketch, "E682.MirrorCS", {"start": v(133.82, 70.59) * mm, "end": v(133.82, 36.2) * mm});
            skLineSegment(sketch, "E683.MirrorCS", {"start": v(295.93, 47.98) * mm, "end": v(295.93, 3) * mm});
            skArc(sketch, "E684.MirrorCS", {"start": v(237.68, 26.62) * mm, "mid": v(253.26, 18.77) * mm, "end": v(260.72, 3) * mm});
            skLineSegment(sketch, "E685.MirrorCS", {"start": v(242.97, 94.64) * mm, "end": v(242.74, 31.81) * mm});
            skArc(sketch, "E686.MirrorCS", {"start": v(265.82, 8.78) * mm, "mid": v(257.33, 23.35) * mm, "end": v(242.74, 31.82) * mm});
            skLineSegment(sketch, "E687.MirrorCS", {"start": v(109.91, 94.64) * mm, "end": v(110.15, 31.81) * mm});
            skLineSegment(sketch, "E688.MirrorCS", {"start": v(296.9, -100.89) * mm, "end": v(315.17, -100.89) * mm});
            skLineSegment(sketch, "E689.MirrorCS", {"start": v(181.64, -75.12) * mm, "end": v(181.64, -100.89) * mm});
            skLineSegment(sketch, "E690.MirrorCS", {"start": v(364.32, 70.59) * mm, "end": v(364.32, 36.2) * mm});
            skLineSegment(sketch, "E691.MirrorCS", {"start": v(181.64, 75.12) * mm, "end": v(181.64, 100.89) * mm});
            skLineSegment(sketch, "E692.MirrorCS", {"start": v(286.5, 75.12) * mm, "end": v(286.5, 100.89) * mm});
            skArc(sketch, "E693.MirrorCS", {"start": v(383.48, 79.48) * mm, "mid": v(393.2, 79.71) * mm, "end": v(401.75, 75.12) * mm});
            skLineSegment(sketch, "E694.MirrorCS", {"start": v(66.39, 75.12) * mm, "end": v(66.39, 100.89) * mm});
            skArc(sketch, "E695.MirrorCS", {"start": v(150.56, 8.78) * mm, "mid": v(142.07, 23.35) * mm, "end": v(127.48, 31.82) * mm});
            skLineSegment(sketch, "E696.MirrorCS", {"start": v(65.42, 47.98) * mm, "end": v(65.42, 3) * mm});
            skArc(sketch, "E697.MirrorCS", {"start": v(381.07, -8.78) * mm, "mid": v(372.58, -23.35) * mm, "end": v(358, -31.82) * mm});
            skArc(sketch, "E698.MirrorCS", {"start": v(202.32, 8.78) * mm, "mid": v(210.8, 23.35) * mm, "end": v(225.4, 31.82) * mm});
            skLineSegment(sketch, "E699.MirrorCS", {"start": v(237.68, -26.62) * mm, "end": v(237.68, -100.89) * mm});
            skLineSegment(sketch, "E700.MirrorCS", {"start": v(334.32, 70.59) * mm, "end": v(334.32, 36.2) * mm});
            skLineSegment(sketch, "E701.MirrorCS", {"start": v(127.72, -94.64) * mm, "end": v(127.48, -31.81) * mm});
            skArc(sketch, "E702.MirrorCS", {"start": v(377.7, -45.33) * mm, "mid": v(369.92, -56.84) * mm, "end": v(371.84, -70.59) * mm});
            skArc(sketch, "E703.MirrorCS", {"start": v(345.71, -26.62) * mm, "mid": v(330.13, -18.77) * mm, "end": v(322.67, -3) * mm});
            skArc(sketch, "E704.MirrorCS", {"start": v(320.95, 45.33) * mm, "mid": v(328.73, 56.84) * mm, "end": v(326.8, 70.59) * mm});
            skLineSegment(sketch, "E705.MirrorCS", {"start": v(358.23, 94.64) * mm, "end": v(358, 31.81) * mm});
            skArc(sketch, "E706.MirrorCS", {"start": v(90.44, 45.33) * mm, "mid": v(98.22, 56.84) * mm, "end": v(96.3, 70.59) * mm});
            skLineSegment(sketch, "E707.MirrorCS", {"start": v(84.66, -79.48) * mm, "end": v(84.66, -100.89) * mm});
            skArc(sketch, "E708.MirrorCS", {"start": v(87.06, 8.78) * mm, "mid": v(95.56, 23.35) * mm, "end": v(110.15, 31.82) * mm});
            skLineSegment(sketch, "E709.MirrorCS", {"start": v(401.75, -75.12) * mm, "end": v(401.75, -100.89) * mm});
            skLineSegment(sketch, "E710.MirrorCS", {"start": v(199.91, -79.48) * mm, "end": v(199.91, -100.89) * mm});
            skArc(sketch, "E711.MirrorCS", {"start": v(352.94, 26.62) * mm, "mid": v(368.52, 18.77) * mm, "end": v(375.98, 3) * mm});
            skArc(sketch, "E712.MirrorCS", {"start": v(262.44, 45.33) * mm, "mid": v(254.66, 56.84) * mm, "end": v(256.59, 70.59) * mm});
            skArc(sketch, "E713.MirrorCS", {"start": v(205.7, 45.33) * mm, "mid": v(213.48, 56.84) * mm, "end": v(211.55, 70.59) * mm});
            skArc(sketch, "E714.MirrorCS", {"start": v(115.2, -26.62) * mm, "mid": v(99.62, -18.77) * mm, "end": v(92.16, -3) * mm});
            skArc(sketch, "E715.MirrorCS", {"start": v(90.44, -45.33) * mm, "mid": v(98.22, -56.84) * mm, "end": v(96.3, -70.59) * mm});
            skLineSegment(sketch, "E716.MirrorCS", {"start": v(295.93, -47.98) * mm, "end": v(295.93, -3) * mm});
            skLineSegment(sketch, "E717.MirrorCS", {"start": v(287.46, 47.98) * mm, "end": v(287.46, 3) * mm});
            skLineSegment(sketch, "E718.MirrorCS", {"start": v(152.97, 79.48) * mm, "end": v(152.97, 100.89) * mm});
            skLineSegment(sketch, "E719.MirrorCS", {"start": v(242.97, -94.64) * mm, "end": v(242.74, -31.81) * mm});
            skArc(sketch, "E720.MirrorCS", {"start": v(265.82, -8.78) * mm, "mid": v(257.33, -23.35) * mm, "end": v(242.74, -31.82) * mm});
            skLineSegment(sketch, "E721.MirrorCS", {"start": v(219.07, -70.59) * mm, "end": v(219.07, -36.2) * mm});
            skArc(sketch, "E722.MirrorCS", {"start": v(202.32, -8.78) * mm, "mid": v(210.8, -23.35) * mm, "end": v(225.4, -31.82) * mm});
            skLineSegment(sketch, "E723.MirrorCS", {"start": v(401.75, -100.89) * mm, "end": v(383.48, -100.89) * mm});
            skLineSegment(sketch, "E724.MirrorCS", {"start": v(172.2, 47.98) * mm, "end": v(172.2, 3) * mm});
            skLineSegment(sketch, "E725.MirrorCS", {"start": v(180.67, 47.98) * mm, "end": v(180.67, 3) * mm});
            skCircle(sketch, "E726.MirrorC", {"center": v(388.77, -61.2) * mm, "radius": 10.77 * mm});
            skCircle(sketch, "E727.MirrorC", {"center": v(79.37, -61.2) * mm, "radius": 10.77 * mm});
            skLineSegment(sketch, "E728.MirrorCS", {"start": v(171.24, -75.12) * mm, "end": v(171.24, -100.89) * mm});
            skLineSegment(sketch, "E729.MirrorCS", {"start": v(103.81, -70.59) * mm, "end": v(103.81, -36.2) * mm});
            skLineSegment(sketch, "E730.MirrorCS", {"start": v(122.43, -26.62) * mm, "end": v(122.43, -100.89) * mm});
            skLineSegment(sketch, "E731.MirrorCS", {"start": v(296.9, 100.89) * mm, "end": v(315.17, 100.89) * mm});
            skLineSegment(sketch, "E732.MirrorCS", {"start": v(287.46, -47.98) * mm, "end": v(287.46, -3) * mm});
            skLineSegment(sketch, "E733.MirrorCS", {"start": v(230.46, 26.62) * mm, "end": v(230.46, 100.89) * mm});
            skArc(sketch, "E734.MirrorCS", {"start": v(150.56, -8.78) * mm, "mid": v(142.07, -23.35) * mm, "end": v(127.48, -31.82) * mm});
            skLineSegment(sketch, "E735.MirrorCS", {"start": v(133.82, -70.59) * mm, "end": v(133.82, -36.2) * mm});
            skLineSegment(sketch, "E736.MirrorCS", {"start": v(172.2, -47.98) * mm, "end": v(172.2, -3) * mm});
            skCircle(sketch, "E737.MirrorC", {"center": v(349.32, 0) * mm, "radius": 20.2 * mm});
            skLineSegment(sketch, "E738.MirrorCS", {"start": v(291.7, -105.78) * mm, "end": v(406.95, -105.78) * mm});
            skLineSegment(sketch, "E739.MirrorCS", {"start": v(291.7, 105.78) * mm, "end": v(406.95, 105.78) * mm});
            skCircle(sketch, "E740.MirrorC", {"center": v(234.07, 0) * mm, "radius": 20.2 * mm});
            skLineSegment(sketch, "E741.MirrorCS", {"start": v(291.7, -105.78) * mm, "end": v(176.44, -105.78) * mm});
            skLineSegment(sketch, "E742.MirrorCS", {"start": v(291.7, 105.78) * mm, "end": v(176.44, 105.78) * mm});
            skCircle(sketch, "E743.MirrorC", {"center": v(118.81, 0) * mm, "radius": 20.2 * mm});
            skLineSegment(sketch, "E744.MirrorCS", {"start": v(61.19, 105.78) * mm, "end": v(176.44, 105.78) * mm});
            skLineSegment(sketch, "E745.MirrorCS", {"start": v(61.19, -105.78) * mm, "end": v(176.44, -105.78) * mm});
            skSolve(sketch);
        }
        {
            var Q0;
            Q0 = qSketchRegion(id + "F0", true);
            extrude(context, id + "F1", {"entities" : qUnion([Q0]), "depth" : 2 * mm, "offsetDistance" : 25.4 * mm});
        }
    });
